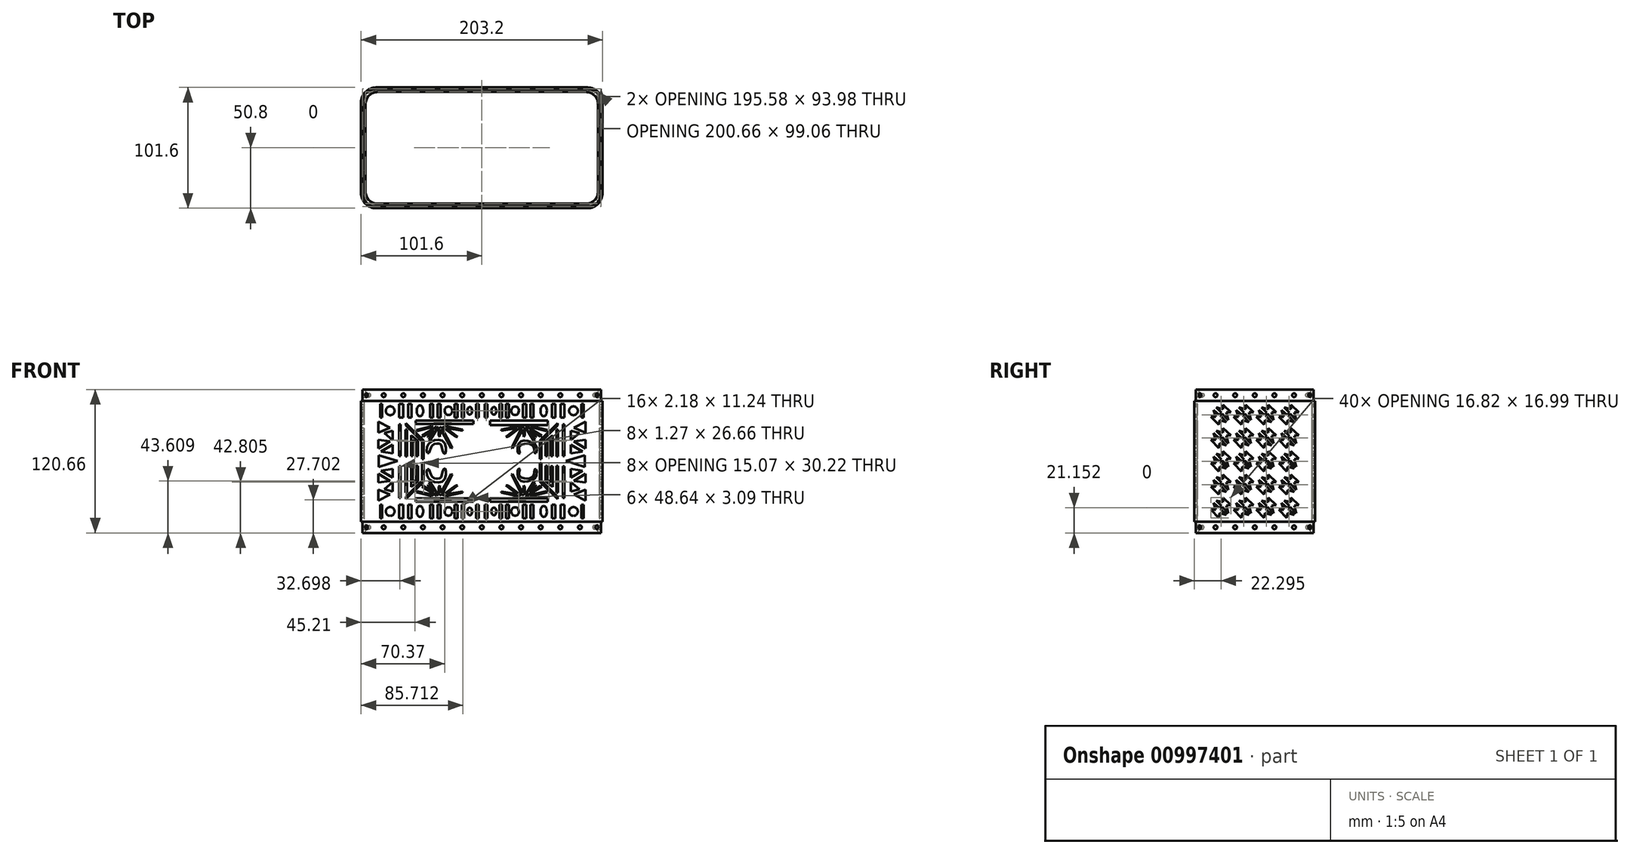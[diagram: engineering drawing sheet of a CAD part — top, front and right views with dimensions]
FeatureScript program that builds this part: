
annotation { "Feature Type Name" : "Feature", "Feature Type Description" : "" }
export const myFeature = defineFeature(function(context is Context, id is Id, definition is map)
    precondition{}
    {
        {
            var Q0;
            Q0=qCreatedBy(makeId("Top.planeOp"),FACE);
            var sketch = newSketch(context, id + "F0", { "sketchPlane" : qUnion([Q0])});
            skLineSegment(sketch, "E0.bottom", {"start": v(-88.9, 50.8) * mm, "end": v(88.9, 50.8) * mm});
            skLineSegment(sketch, "E0.top", {"start": v(-88.9, -50.8) * mm, "end": v(88.9, -50.8) * mm});
            skLineSegment(sketch, "E0.left", {"start": v(-101.6, 38.1) * mm, "end": v(-101.6, -38.1) * mm});
            skLineSegment(sketch, "E0.right", {"start": v(101.6, 38.1) * mm, "end": v(101.6, -38.1) * mm});
            skPoint(sketch, "E1.visualSharp", {"position": v(-101.6, -50.8) * mm});
            skArc(sketch, "E1.filletArc", {"start": v(-101.6, -38.1) * mm, "mid": v(-97.88, -47.08) * mm, "end": v(-88.9, -50.8) * mm});
            skPoint(sketch, "E2.visualSharp", {"position": v(101.6, -50.8) * mm});
            skArc(sketch, "E2.filletArc", {"start": v(88.9, -50.8) * mm, "mid": v(97.88, -47.08) * mm, "end": v(101.6, -38.1) * mm});
            skPoint(sketch, "E3.visualSharp", {"position": v(-101.6, 50.8) * mm});
            skArc(sketch, "E3.filletArc", {"start": v(-88.9, 50.8) * mm, "mid": v(-97.88, 47.08) * mm, "end": v(-101.6, 38.1) * mm});
            skPoint(sketch, "E4.visualSharp", {"position": v(101.6, 50.8) * mm});
            skArc(sketch, "E4.filletArc", {"start": v(101.6, 38.1) * mm, "mid": v(97.88, 47.08) * mm, "end": v(88.9, 50.8) * mm});
            skSolve(sketch);
        }
        {
            var Q0;
            Q0=makeQuery(id+"F0.imprint","IMPRINT",FACE,{"disambiguationData":[TD([[makeQuery(id+"F0.imprint","IMPRINT",EDGE,{"derivedFrom":sQuery(id+"F0.wireOp",EDGE,"E0.bottom")}),-1.0]])]});
            extrude(context, id + "F1", {"entities" : qUnion([Q0]), "depth" : 101.6 * mm, "offsetDistance" : 25.4 * mm});
        }
        {
            var Q0;
            Q0=makeQuery(id+"F1.opExtrude","CAP_FACE",FACE,{"disambiguationData":[OSD([sQuery(id+"F0.wireOp",EDGE,"E0.bottom"),sQuery(id+"F0.wireOp",EDGE,"E0.top"),sQuery(id+"F0.wireOp",EDGE,"E0.left"),sQuery(id+"F0.wireOp",EDGE,"E0.right"),sQuery(id+"F0.wireOp",EDGE,"E1.filletArc"),sQuery(id+"F0.wireOp",EDGE,"E2.filletArc"),sQuery(id+"F0.wireOp",EDGE,"E3.filletArc"),sQuery(id+"F0.wireOp",EDGE,"E4.filletArc")])],"isStart":false});
            var Q1;
            Q1=makeQuery(id+"F1.opExtrude","CAP_FACE",FACE,{"disambiguationData":[OSD([sQuery(id+"F0.wireOp",EDGE,"E0.bottom"),sQuery(id+"F0.wireOp",EDGE,"E0.top"),sQuery(id+"F0.wireOp",EDGE,"E0.left"),sQuery(id+"F0.wireOp",EDGE,"E0.right"),sQuery(id+"F0.wireOp",EDGE,"E1.filletArc"),sQuery(id+"F0.wireOp",EDGE,"E2.filletArc"),sQuery(id+"F0.wireOp",EDGE,"E3.filletArc"),sQuery(id+"F0.wireOp",EDGE,"E4.filletArc")])],"isStart":true});
            shell(context, id + "F2", {"entities" : qUnion([Q0, Q1]), "thickness" : 2.54 * mm});
        }
        {
            var Q0;
            Q0=makeQuery(id+"F1.opExtrude","CAP_FACE",FACE,{"disambiguationData":[OSD([sQuery(id+"F0.wireOp",EDGE,"E0.bottom"),sQuery(id+"F0.wireOp",EDGE,"E0.top"),sQuery(id+"F0.wireOp",EDGE,"E0.left"),sQuery(id+"F0.wireOp",EDGE,"E0.right"),sQuery(id+"F0.wireOp",EDGE,"E1.filletArc"),sQuery(id+"F0.wireOp",EDGE,"E2.filletArc"),sQuery(id+"F0.wireOp",EDGE,"E3.filletArc"),sQuery(id+"F0.wireOp",EDGE,"E4.filletArc")])],"isStart":false});
            var sketch = newSketch(context, id + "F3", { "sketchPlane" : qUnion([Q0])});
            skLineSegment(sketch, "E5.bottom", {"start": v(88.9, -49.53) * mm, "end": v(-88.9, -49.53) * mm});
            skLineSegment(sketch, "E5.top", {"start": v(88.9, 49.53) * mm, "end": v(-88.9, 49.53) * mm});
            skLineSegment(sketch, "E5.left", {"start": v(100.33, -38.1) * mm, "end": v(100.33, 38.1) * mm});
            skLineSegment(sketch, "E5.right", {"start": v(-100.33, -38.1) * mm, "end": v(-100.33, 38.1) * mm});
            skPoint(sketch, "E5.middle", {"position": v(0, 0) * mm});
            skPoint(sketch, "E6.visualSharp", {"position": v(-100.33, 49.53) * mm});
            skArc(sketch, "E6.filletArc", {"start": v(-88.9, 49.53) * mm, "mid": v(-96.98, 46.18) * mm, "end": v(-100.33, 38.1) * mm});
            skPoint(sketch, "E7.visualSharp", {"position": v(100.33, 49.53) * mm});
            skArc(sketch, "E7.filletArc", {"start": v(100.33, 38.1) * mm, "mid": v(96.98, 46.18) * mm, "end": v(88.9, 49.53) * mm});
            skPoint(sketch, "E8.visualSharp", {"position": v(100.33, -49.53) * mm});
            skArc(sketch, "E8.filletArc", {"start": v(88.9, -49.53) * mm, "mid": v(96.98, -46.18) * mm, "end": v(100.33, -38.1) * mm});
            skPoint(sketch, "E9.visualSharp", {"position": v(-100.33, -49.53) * mm});
            skArc(sketch, "E9.filletArc", {"start": v(-100.33, -38.1) * mm, "mid": v(-96.98, -46.18) * mm, "end": v(-88.9, -49.53) * mm});
            skLineSegment(sketch, "E10.bottom", {"start": v(-87.63, 46.99) * mm, "end": v(87.63, 47) * mm});
            skLineSegment(sketch, "E10.top", {"start": v(-87.63, -47) * mm, "end": v(87.63, -46.99) * mm});
            skLineSegment(sketch, "E10.left", {"start": v(-97.8, 36.83) * mm, "end": v(-97.8, -36.83) * mm});
            skLineSegment(sketch, "E10.right", {"start": v(97.8, 36.83) * mm, "end": v(97.8, -36.83) * mm});
            skPoint(sketch, "E11.visualSharp", {"position": v(-97.8, -47) * mm});
            skArc(sketch, "E11.filletArc", {"start": v(-97.8, -36.83) * mm, "mid": v(-94.81, -44.01) * mm, "end": v(-87.63, -47) * mm});
            skPoint(sketch, "E12.visualSharp", {"position": v(-97.8, 46.99) * mm});
            skArc(sketch, "E12.filletArc", {"start": v(-87.63, 47) * mm, "mid": v(-94.81, 44.01) * mm, "end": v(-97.8, 36.83) * mm});
            skPoint(sketch, "E13.visualSharp", {"position": v(97.8, 47) * mm});
            skArc(sketch, "E13.filletArc", {"start": v(97.8, 36.83) * mm, "mid": v(94.81, 44.01) * mm, "end": v(87.63, 47) * mm});
            skPoint(sketch, "E14.visualSharp", {"position": v(97.8, -46.99) * mm});
            skArc(sketch, "E14.filletArc", {"start": v(87.63, -46.99) * mm, "mid": v(94.81, -44.01) * mm, "end": v(97.8, -36.83) * mm});
            skSolve(sketch);
        }
        {
            var Q0;
            Q0=makeQuery(id+"F3.imprint","IMPRINT",FACE,{"disambiguationData":[TD([[makeQuery(id+"F3.imprint","IMPRINT",EDGE,{"derivedFrom":sQuery(id+"F3.wireOp",EDGE,"E10.bottom")}),1.0]])]});
            var Q1;
            Q1=makeQuery(id+"F3.imprint","IMPRINT",FACE,{"disambiguationData":[TD([[makeQuery(id+"F3.imprint","IMPRINT",EDGE,{"derivedFrom":sQuery(id+"F3.wireOp",EDGE,"E5.bottom")}),-1.0]])]});
            extrude(context, id + "F4", {"entities" : qUnion([Q0, Q1]), "operationType" : NewBodyOperationType.ADD, "depth" : 9.52 * mm, "offsetDistance" : 25.4 * mm});
        }
        {
            var Q0;
            Q0=qCreatedBy(makeId("Top.planeOp"),FACE);
            var sketch = newSketch(context, id + "F5", { "sketchPlane" : qUnion([Q0])});
            skLineSegment(sketch, "E15.bottom", {"start": v(-88.9, 49.53) * mm, "end": v(88.9, 49.53) * mm});
            skLineSegment(sketch, "E15.top", {"start": v(-88.9, -49.53) * mm, "end": v(88.9, -49.53) * mm});
            skLineSegment(sketch, "E15.left", {"start": v(-100.33, 38.1) * mm, "end": v(-100.33, -38.1) * mm});
            skLineSegment(sketch, "E15.right", {"start": v(100.33, 38.1) * mm, "end": v(100.33, -38.1) * mm});
            skPoint(sketch, "E15.middle", {"position": v(0, 0) * mm});
            skLineSegment(sketch, "E16.bottom", {"start": v(-87.63, -47) * mm, "end": v(87.63, -46.99) * mm});
            skLineSegment(sketch, "E16.top", {"start": v(-87.63, 46.99) * mm, "end": v(87.63, 47) * mm});
            skLineSegment(sketch, "E16.left", {"start": v(-97.8, -36.83) * mm, "end": v(-97.8, 36.83) * mm});
            skLineSegment(sketch, "E16.right", {"start": v(97.8, -36.83) * mm, "end": v(97.8, 36.83) * mm});
            skPoint(sketch, "E17.visualSharp", {"position": v(97.8, 47) * mm});
            skArc(sketch, "E17.filletArc", {"start": v(97.8, 36.83) * mm, "mid": v(94.81, 44.01) * mm, "end": v(87.63, 47) * mm});
            skPoint(sketch, "E18.visualSharp", {"position": v(-97.8, 46.99) * mm});
            skArc(sketch, "E18.filletArc", {"start": v(-87.63, 46.99) * mm, "mid": v(-94.81, 44.01) * mm, "end": v(-97.79, 36.83) * mm});
            skPoint(sketch, "E19.visualSharp", {"position": v(-97.8, -47) * mm});
            skArc(sketch, "E19.filletArc", {"start": v(-97.8, -36.83) * mm, "mid": v(-94.81, -44.01) * mm, "end": v(-87.63, -47) * mm});
            skPoint(sketch, "E20.visualSharp", {"position": v(97.8, -46.99) * mm});
            skArc(sketch, "E20.filletArc", {"start": v(87.63, -46.99) * mm, "mid": v(94.81, -44.01) * mm, "end": v(97.79, -36.83) * mm});
            skPoint(sketch, "E21.visualSharp", {"position": v(100.33, -49.53) * mm});
            skArc(sketch, "E21.filletArc", {"start": v(88.9, -49.53) * mm, "mid": v(96.98, -46.18) * mm, "end": v(100.33, -38.1) * mm});
            skPoint(sketch, "E22.visualSharp", {"position": v(-100.33, -49.53) * mm});
            skArc(sketch, "E22.filletArc", {"start": v(-100.33, -38.1) * mm, "mid": v(-96.98, -46.18) * mm, "end": v(-88.9, -49.53) * mm});
            skPoint(sketch, "E23.visualSharp", {"position": v(-100.33, 49.53) * mm});
            skArc(sketch, "E23.filletArc", {"start": v(-88.9, 49.53) * mm, "mid": v(-96.98, 46.18) * mm, "end": v(-100.33, 38.1) * mm});
            skPoint(sketch, "E24.visualSharp", {"position": v(100.33, 49.53) * mm});
            skArc(sketch, "E24.filletArc", {"start": v(100.33, 38.1) * mm, "mid": v(96.98, 46.18) * mm, "end": v(88.9, 49.53) * mm});
            skSolve(sketch);
        }
        {
            var Q0;
            Q0 = qSketchRegion(id + "F5", true);
            extrude(context, id + "F6", {"entities" : qUnion([Q0]), "operationType" : NewBodyOperationType.ADD, "oppositeDirection" : true, "depth" : 9.52 * mm, "offsetDistance" : 25.4 * mm});
        }
        {
            var Q0;
            Q0=makeQuery(id+"F1.opExtrude","SWEPT_FACE",FACE,{"disambiguationData":[OSD([sQuery(id+"F0.wireOp",EDGE,"E0.top")])]});
            var sketch = newSketch(context, id + "F7", { "sketchPlane" : qUnion([Q0])});
            skPoint(sketch, "E25", {"position": v(-82.55, 50.8) * mm});
            skPoint(sketch, "E26", {"position": v(82.55, 50.8) * mm});
            skPoint(sketch, "E27", {"position": v(88.9, 50.8) * mm});
            skPoint(sketch, "E28", {"position": v(-88.9, 50.8) * mm});
            skPoint(sketch, "E29", {"position": v(0, 101.6) * mm});
            skPoint(sketch, "E30", {"position": v(0, 97.17) * mm});
            skSolve(sketch);
        }
        {
            var Q0;
            {var subQ0=sQuery(id+"F0.wireOp",EDGE,"E0.top");Q0=makeQuery(id+"F7.imprint","IMPRINT",FACE,{"disambiguationData":[TD([[makeQuery(id+"F7.imprint","IMPRINT",EDGE,{"derivedFrom":makeQuery(id+"F1.opExtrude","CAP_EDGE",EDGE,{"disambiguationData":[OSD([subQ0])],"isStart":true})}),1.0]])]});}
            var sketch = newSketch(context, id + "F8", { "sketchPlane" : qUnion([Q0])});
            skLineSegment(sketch, "E31.bottom", {"start": v(-69.54, 81.8) * mm, "end": v(-68.27, 81.8) * mm});
            skLineSegment(sketch, "E31.top", {"start": v(-69.54, 55.15) * mm, "end": v(-68.27, 55.15) * mm});
            skLineSegment(sketch, "E31.left", {"start": v(-69.54, 81.8) * mm, "end": v(-69.54, 55.15) * mm});
            skLineSegment(sketch, "E31.right", {"start": v(-68.27, 81.8) * mm, "end": v(-68.27, 55.15) * mm});
            skLineSegment(sketch, "E32.bottom", {"start": v(-64.12, 77.24) * mm, "end": v(-62.85, 77.24) * mm});
            skLineSegment(sketch, "E32.top", {"start": v(-64.12, 55) * mm, "end": v(-62.85, 55) * mm});
            skLineSegment(sketch, "E32.left", {"start": v(-64.12, 77.24) * mm, "end": v(-64.12, 55) * mm});
            skLineSegment(sketch, "E32.right", {"start": v(-62.85, 77.24) * mm, "end": v(-62.85, 55) * mm});
            skLineSegment(sketch, "E33", {"start": v(-59.53, 55.07) * mm, "end": v(-59.53, 72.59) * mm});
            skLineSegment(sketch, "E34", {"start": v(-59.53, 72.59) * mm, "end": v(-53.58, 67.88) * mm});
            skLineSegment(sketch, "E35", {"start": v(-53.58, 67.88) * mm, "end": v(-53.58, 55) * mm});
            skLineSegment(sketch, "E36", {"start": v(-53.58, 55) * mm, "end": v(-55.15, 55) * mm});
            skLineSegment(sketch, "E37", {"start": v(-55.15, 55) * mm, "end": v(-55.15, 66.64) * mm});
            skLineSegment(sketch, "E38", {"start": v(-55.15, 66.64) * mm, "end": v(-58.16, 68.8) * mm});
            skLineSegment(sketch, "E39", {"start": v(-59.53, 55.07) * mm, "end": v(-58.16, 55.07) * mm});
            skLineSegment(sketch, "E40", {"start": v(-58.16, 55.07) * mm, "end": v(-58.16, 68.8) * mm});
            skLineSegment(sketch, "E41", {"start": v(-50.14, 52.56) * mm, "end": v(-50.14, 67.28) * mm});
            skLineSegment(sketch, "E42", {"start": v(-50.14, 67.28) * mm, "end": v(-63.92, 80.98) * mm});
            skLineSegment(sketch, "E43", {"start": v(-63.92, 80.98) * mm, "end": v(-63.92, 82.78) * mm});
            skLineSegment(sketch, "E44", {"start": v(-63.92, 82.78) * mm, "end": v(-48.86, 68.23) * mm});
            skLineSegment(sketch, "E45", {"start": v(-48.86, 68.23) * mm, "end": v(-48.86, 52.56) * mm});
            skLineSegment(sketch, "E46", {"start": v(-48.86, 52.56) * mm, "end": v(-50.14, 52.56) * mm});
            skLineSegment(sketch, "E47.bottom", {"start": v(-55.55, 82.03) * mm, "end": v(-6.91, 82.03) * mm});
            skLineSegment(sketch, "E47.top", {"start": v(-55.55, 85.13) * mm, "end": v(-6.91, 85.13) * mm});
            skLineSegment(sketch, "E47.left", {"start": v(-55.55, 82.03) * mm, "end": v(-55.55, 85.13) * mm});
            skLineSegment(sketch, "E47.right", {"start": v(-6.91, 82.03) * mm, "end": v(-6.91, 85.13) * mm});
            skLineSegment(sketch, "E48", {"start": v(-55.1, 76.98) * mm, "end": v(-42.24, 80.13) * mm});
            skLineSegment(sketch, "E49", {"start": v(-42.24, 80.13) * mm, "end": v(-40.9, 79.45) * mm});
            skLineSegment(sketch, "E50", {"start": v(-40.9, 79.45) * mm, "end": v(-54.58, 76.07) * mm});
            skLineSegment(sketch, "E51", {"start": v(-54.58, 76.07) * mm, "end": v(-55.1, 76.98) * mm});
            skLineSegment(sketch, "E52", {"start": v(-50.33, 72.34) * mm, "end": v(-49.32, 71.33) * mm});
            skLineSegment(sketch, "E53", {"start": v(-49.32, 71.33) * mm, "end": v(-40.54, 77.24) * mm});
            skLineSegment(sketch, "E54", {"start": v(-40.54, 77.24) * mm, "end": v(-45.9, 71.84) * mm});
            skLineSegment(sketch, "E55", {"start": v(-45.9, 71.84) * mm, "end": v(-45.04, 70.98) * mm});
            skLineSegment(sketch, "E56", {"start": v(-45.04, 70.98) * mm, "end": v(-40.01, 76.03) * mm});
            skLineSegment(sketch, "E57", {"start": v(-40.01, 76.03) * mm, "end": v(-44.6, 68.93) * mm});
            skLineSegment(sketch, "E58", {"start": v(-44.6, 68.93) * mm, "end": v(-43.9, 67.87) * mm});
            skLineSegment(sketch, "E59", {"start": v(-43.9, 67.87) * mm, "end": v(-36.86, 79.28) * mm});
            skLineSegment(sketch, "E60", {"start": v(-36.86, 79.28) * mm, "end": v(-37.94, 79.94) * mm});
            skLineSegment(sketch, "E61", {"start": v(-37.94, 79.94) * mm, "end": v(-50.33, 72.34) * mm});
            skLineSegment(sketch, "E62", {"start": v(-36.28, 72.34) * mm, "end": v(-35.26, 71.33) * mm});
            skLineSegment(sketch, "E63", {"start": v(-34.02, 79.8) * mm, "end": v(-36.11, 78.38) * mm});
            skLineSegment(sketch, "E64", {"start": v(-36.11, 78.38) * mm, "end": v(-36.28, 72.34) * mm});
            skLineSegment(sketch, "E65", {"start": v(-34.02, 79.8) * mm, "end": v(-24.97, 62.28) * mm});
            skLineSegment(sketch, "E66", {"start": v(-24.97, 62.28) * mm, "end": v(-25.62, 61.62) * mm});
            skLineSegment(sketch, "E67", {"start": v(-22.03, 71.33) * mm, "end": v(-20.4, 71.33) * mm});
            skLineSegment(sketch, "E68", {"start": v(-20.4, 71.33) * mm, "end": v(-29.91, 78.67) * mm});
            skLineSegment(sketch, "E69", {"start": v(-29.91, 78.67) * mm, "end": v(-16.35, 76.46) * mm});
            skLineSegment(sketch, "E70", {"start": v(-16.35, 76.46) * mm, "end": v(-16.35, 77.5) * mm});
            skLineSegment(sketch, "E71", {"start": v(-16.35, 77.5) * mm, "end": v(-29.9, 80.27) * mm});
            skLineSegment(sketch, "E72", {"start": v(-29.9, 80.27) * mm, "end": v(-32.77, 79.37) * mm});
            skFitSpline(sketch, "E73", {"points": [v(-45.65, 57.64) * mm, v(-45.68, 63.84) * mm, v(-39.17, 68.5) * mm, v(-31.43, 66.27) * mm, v(-30.64, 57.48) * mm, v(-32.02, 57.42) * mm, v(-33.93, 63.5) * mm, v(-35.4, 65.37) * mm, v(-39.79, 65.41) * mm, v(-43.04, 61.77) * mm, v(-44.66, 57.59) * mm, v(-45.65, 57.64) * mm]});
            skLineSegment(sketch, "E74", {"start": v(-25.62, 61.62) * mm, "end": v(-34.64, 77.63) * mm});
            skLineSegment(sketch, "E75", {"start": v(-34.64, 77.63) * mm, "end": v(-35.26, 71.33) * mm});
            skLineSegment(sketch, "E76", {"start": v(-22.03, 71.33) * mm, "end": v(-32.77, 79.37) * mm});
            skLineSegment(sketch, "E77.MirrorCS", {"start": v(50.33, 72.34) * mm, "end": v(49.32, 71.33) * mm});
            skLineSegment(sketch, "E78.MirrorCS", {"start": v(36.86, 79.28) * mm, "end": v(37.94, 79.94) * mm});
            skLineSegment(sketch, "E79.MirrorCS", {"start": v(63.92, 80.98) * mm, "end": v(63.92, 82.78) * mm});
            skLineSegment(sketch, "E80.MirrorCS", {"start": v(45.9, 71.84) * mm, "end": v(45.04, 70.98) * mm});
            skLineSegment(sketch, "E81.MirrorCS", {"start": v(59.53, 55.07) * mm, "end": v(58.16, 55.07) * mm});
            skLineSegment(sketch, "E82.MirrorCS", {"start": v(55.55, 81.06) * mm, "end": v(55.55, 85.13) * mm});
            skLineSegment(sketch, "E83.MirrorCS", {"start": v(36.28, 72.34) * mm, "end": v(35.26, 71.33) * mm});
            skLineSegment(sketch, "E84.MirrorCS", {"start": v(53.58, 55) * mm, "end": v(55.15, 55) * mm});
            skLineSegment(sketch, "E85.MirrorCS", {"start": v(29.9, 80.27) * mm, "end": v(32.77, 79.37) * mm});
            skLineSegment(sketch, "E86.MirrorCS", {"start": v(34.64, 77.63) * mm, "end": v(35.26, 71.33) * mm});
            skLineSegment(sketch, "E87.MirrorCS", {"start": v(64.12, 55) * mm, "end": v(62.85, 55) * mm});
            skLineSegment(sketch, "E88.MirrorCS", {"start": v(69.54, 55.15) * mm, "end": v(68.27, 55.15) * mm});
            skLineSegment(sketch, "E89.MirrorCS", {"start": v(44.6, 68.93) * mm, "end": v(43.9, 67.87) * mm});
            skLineSegment(sketch, "E90.MirrorCS", {"start": v(54.58, 76.07) * mm, "end": v(55.1, 76.98) * mm});
            skLineSegment(sketch, "E91.MirrorCS", {"start": v(24.97, 62.28) * mm, "end": v(25.62, 61.62) * mm});
            skLineSegment(sketch, "E92.MirrorCS", {"start": v(16.35, 76.46) * mm, "end": v(16.35, 77.5) * mm});
            skLineSegment(sketch, "E93.MirrorCS", {"start": v(6.91, 81.06) * mm, "end": v(6.91, 85.13) * mm});
            skLineSegment(sketch, "E94.MirrorCS", {"start": v(55.15, 66.64) * mm, "end": v(58.16, 68.8) * mm});
            skLineSegment(sketch, "E95.MirrorCS", {"start": v(45.04, 70.98) * mm, "end": v(40.01, 76.03) * mm});
            skLineSegment(sketch, "E96.MirrorCS", {"start": v(59.53, 72.59) * mm, "end": v(53.58, 67.88) * mm});
            skLineSegment(sketch, "E97.MirrorCS", {"start": v(64.12, 77.24) * mm, "end": v(62.85, 77.24) * mm});
            skLineSegment(sketch, "E98.MirrorCS", {"start": v(22.03, 71.33) * mm, "end": v(20.4, 71.33) * mm});
            skLineSegment(sketch, "E99.MirrorCS", {"start": v(36.11, 78.38) * mm, "end": v(36.28, 72.34) * mm});
            skLineSegment(sketch, "E100.MirrorCS", {"start": v(69.54, 81.8) * mm, "end": v(68.27, 81.8) * mm});
            skLineSegment(sketch, "E101.MirrorCS", {"start": v(34.02, 79.8) * mm, "end": v(36.11, 78.38) * mm});
            skLineSegment(sketch, "E102.MirrorCS", {"start": v(42.24, 80.13) * mm, "end": v(40.9, 79.45) * mm});
            skLineSegment(sketch, "E103.MirrorCS", {"start": v(48.86, 52.56) * mm, "end": v(50.14, 52.56) * mm});
            skLineSegment(sketch, "E104.MirrorCS", {"start": v(49.32, 71.33) * mm, "end": v(40.54, 77.24) * mm});
            skLineSegment(sketch, "E105.MirrorCS", {"start": v(64.12, 77.24) * mm, "end": v(64.12, 55) * mm});
            skFitSpline(sketch, "E106.MirrorC", {"points": [v(45.65, 57.64) * mm, v(45.68, 63.84) * mm, v(38.4, 67.98) * mm, v(31.43, 66.27) * mm, v(30.64, 57.48) * mm, v(32.02, 57.42) * mm, v(31.25, 62.15) * mm, v(35.4, 65.37) * mm, v(39.79, 65.41) * mm, v(43.58, 62.94) * mm, v(44.66, 57.59) * mm, v(45.65, 57.64) * mm]});
            skLineSegment(sketch, "E107.MirrorCS", {"start": v(55.55, 81.06) * mm, "end": v(6.91, 81.06) * mm});
            skLineSegment(sketch, "E108.MirrorCS", {"start": v(40.9, 79.45) * mm, "end": v(54.58, 76.07) * mm});
            skLineSegment(sketch, "E109.MirrorCS", {"start": v(55.15, 55) * mm, "end": v(55.15, 66.64) * mm});
            skLineSegment(sketch, "E110.MirrorCS", {"start": v(58.16, 55.07) * mm, "end": v(58.16, 68.8) * mm});
            skLineSegment(sketch, "E111.MirrorCS", {"start": v(55.55, 85.13) * mm, "end": v(6.91, 85.13) * mm});
            skLineSegment(sketch, "E112.MirrorCS", {"start": v(63.92, 82.78) * mm, "end": v(48.86, 68.23) * mm});
            skLineSegment(sketch, "E113.MirrorCS", {"start": v(34.02, 79.8) * mm, "end": v(24.97, 62.28) * mm});
            skLineSegment(sketch, "E114.MirrorCS", {"start": v(50.14, 67.28) * mm, "end": v(63.92, 80.98) * mm});
            skLineSegment(sketch, "E115.MirrorCS", {"start": v(59.53, 55.07) * mm, "end": v(59.53, 72.59) * mm});
            skLineSegment(sketch, "E116.MirrorCS", {"start": v(68.27, 81.8) * mm, "end": v(68.27, 55.15) * mm});
            skLineSegment(sketch, "E117.MirrorCS", {"start": v(40.54, 77.24) * mm, "end": v(45.9, 71.84) * mm});
            skLineSegment(sketch, "E118.MirrorCS", {"start": v(62.85, 77.24) * mm, "end": v(62.85, 55) * mm});
            skLineSegment(sketch, "E119.MirrorCS", {"start": v(16.35, 77.5) * mm, "end": v(29.9, 80.27) * mm});
            skLineSegment(sketch, "E120.MirrorCS", {"start": v(29.91, 78.67) * mm, "end": v(16.35, 76.46) * mm});
            skLineSegment(sketch, "E121.MirrorCS", {"start": v(40.01, 76.03) * mm, "end": v(44.6, 68.93) * mm});
            skLineSegment(sketch, "E122.MirrorCS", {"start": v(25.62, 61.62) * mm, "end": v(34.64, 77.63) * mm});
            skLineSegment(sketch, "E123.MirrorCS", {"start": v(43.9, 67.87) * mm, "end": v(36.86, 79.28) * mm});
            skLineSegment(sketch, "E124.MirrorCS", {"start": v(69.54, 81.8) * mm, "end": v(69.54, 55.15) * mm});
            skLineSegment(sketch, "E125.MirrorCS", {"start": v(48.86, 68.23) * mm, "end": v(48.86, 52.56) * mm});
            skLineSegment(sketch, "E126.MirrorCS", {"start": v(50.14, 52.56) * mm, "end": v(50.14, 67.28) * mm});
            skLineSegment(sketch, "E127.MirrorCS", {"start": v(55.1, 76.98) * mm, "end": v(42.24, 80.13) * mm});
            skLineSegment(sketch, "E128.MirrorCS", {"start": v(37.94, 79.94) * mm, "end": v(50.33, 72.34) * mm});
            skLineSegment(sketch, "E129.MirrorCS", {"start": v(22.03, 71.33) * mm, "end": v(32.77, 79.37) * mm});
            skLineSegment(sketch, "E130.MirrorCS", {"start": v(53.58, 67.88) * mm, "end": v(53.58, 55) * mm});
            skLineSegment(sketch, "E131.MirrorCS", {"start": v(20.4, 71.33) * mm, "end": v(29.91, 78.67) * mm});
            skLineSegment(sketch, "E132", {"start": v(0, 50.88) * mm, "end": v(-88.8, 50.88) * mm, "construction": true});
            skLineSegment(sketch, "E133.MirrorCS", {"start": v(-48.86, 49.19) * mm, "end": v(-50.14, 49.19) * mm});
            skLineSegment(sketch, "E134.MirrorCS", {"start": v(-48.86, 33.53) * mm, "end": v(-48.86, 49.19) * mm});
            skLineSegment(sketch, "E135.MirrorCS", {"start": v(-50.14, 49.19) * mm, "end": v(-50.14, 34.47) * mm});
            skLineSegment(sketch, "E136.MirrorCS", {"start": v(-53.58, 46.75) * mm, "end": v(-55.15, 46.75) * mm});
            skLineSegment(sketch, "E137.MirrorCS", {"start": v(-55.15, 46.75) * mm, "end": v(-55.15, 35.11) * mm});
            skLineSegment(sketch, "E138.MirrorCS", {"start": v(-53.58, 33.87) * mm, "end": v(-53.58, 46.75) * mm});
            skLineSegment(sketch, "E139.MirrorCS", {"start": v(-58.16, 46.68) * mm, "end": v(-58.16, 32.95) * mm});
            skLineSegment(sketch, "E140.MirrorCS", {"start": v(-59.53, 46.68) * mm, "end": v(-58.16, 46.68) * mm});
            skLineSegment(sketch, "E141.MirrorCS", {"start": v(-59.53, 46.68) * mm, "end": v(-59.53, 29.16) * mm});
            skLineSegment(sketch, "E142.MirrorCS", {"start": v(-62.85, 24.52) * mm, "end": v(-62.85, 46.76) * mm});
            skLineSegment(sketch, "E143.MirrorCS", {"start": v(-64.12, 24.52) * mm, "end": v(-64.12, 46.76) * mm});
            skLineSegment(sketch, "E144.MirrorCS", {"start": v(-64.12, 46.76) * mm, "end": v(-62.85, 46.76) * mm});
            skLineSegment(sketch, "E145.MirrorCS", {"start": v(-69.54, 46.6) * mm, "end": v(-68.27, 46.6) * mm});
            skLineSegment(sketch, "E146.MirrorCS", {"start": v(-69.54, 19.94) * mm, "end": v(-69.54, 46.6) * mm});
            skLineSegment(sketch, "E147.MirrorCS", {"start": v(-68.27, 19.94) * mm, "end": v(-68.27, 46.6) * mm});
            skLineSegment(sketch, "E148.MirrorCS", {"start": v(-34.02, 21.96) * mm, "end": v(-36.11, 23.37) * mm});
            skLineSegment(sketch, "E149.MirrorCS", {"start": v(-29.9, 21.48) * mm, "end": v(-32.77, 22.38) * mm});
            skLineSegment(sketch, "E150.MirrorCS", {"start": v(-50.33, 29.41) * mm, "end": v(-49.32, 30.42) * mm});
            skLineSegment(sketch, "E151.MirrorCS", {"start": v(-55.55, 19.72) * mm, "end": v(-55.55, 16.63) * mm});
            skLineSegment(sketch, "E152.MirrorCS", {"start": v(-16.35, 25.3) * mm, "end": v(-16.35, 24.25) * mm});
            skLineSegment(sketch, "E153.MirrorCS", {"start": v(-22.03, 30.42) * mm, "end": v(-20.4, 30.42) * mm});
            skLineSegment(sketch, "E154.MirrorCS", {"start": v(-24.97, 39.48) * mm, "end": v(-25.62, 40.13) * mm});
            skLineSegment(sketch, "E155.MirrorCS", {"start": v(-69.54, 19.94) * mm, "end": v(-68.27, 19.94) * mm});
            skLineSegment(sketch, "E156.MirrorCS", {"start": v(-63.92, 20.77) * mm, "end": v(-63.92, 18.97) * mm});
            skLineSegment(sketch, "E157.MirrorCS", {"start": v(-6.91, 19.72) * mm, "end": v(-6.91, 16.63) * mm});
            skLineSegment(sketch, "E158.MirrorCS", {"start": v(-55.15, 35.11) * mm, "end": v(-58.16, 32.95) * mm});
            skLineSegment(sketch, "E159.MirrorCS", {"start": v(-44.6, 32.83) * mm, "end": v(-43.9, 33.88) * mm});
            skLineSegment(sketch, "E160.MirrorCS", {"start": v(-42.24, 21.62) * mm, "end": v(-40.9, 22.3) * mm});
            skLineSegment(sketch, "E161.MirrorCS", {"start": v(-36.28, 29.41) * mm, "end": v(-35.26, 30.42) * mm});
            skLineSegment(sketch, "E162.MirrorCS", {"start": v(-45.9, 29.92) * mm, "end": v(-45.04, 30.78) * mm});
            skLineSegment(sketch, "E163.MirrorCS", {"start": v(-64.12, 24.52) * mm, "end": v(-62.85, 24.52) * mm});
            skLineSegment(sketch, "E164.MirrorCS", {"start": v(-54.58, 25.68) * mm, "end": v(-55.1, 24.77) * mm});
            skLineSegment(sketch, "E165.MirrorCS", {"start": v(-36.86, 22.48) * mm, "end": v(-37.94, 21.81) * mm});
            skLineSegment(sketch, "E166.MirrorCS", {"start": v(-40.01, 25.72) * mm, "end": v(-44.6, 32.83) * mm});
            skLineSegment(sketch, "E167.MirrorCS", {"start": v(-36.11, 23.37) * mm, "end": v(-36.28, 29.41) * mm});
            skFitSpline(sketch, "E168.MirrorC", {"points": [v(-45.65, 44.1) * mm, v(-45.68, 37.91) * mm, v(-39.17, 33.24) * mm, v(-31.43, 35.48) * mm, v(-30.64, 44.27) * mm, v(-32.02, 44.33) * mm, v(-33.93, 38.25) * mm, v(-35.4, 36.38) * mm, v(-39.79, 36.34) * mm, v(-43.04, 39.98) * mm, v(-44.66, 44.16) * mm, v(-45.65, 44.1) * mm]});
            skLineSegment(sketch, "E169.MirrorCS", {"start": v(-40.54, 24.52) * mm, "end": v(-45.9, 29.92) * mm});
            skLineSegment(sketch, "E170.MirrorCS", {"start": v(-34.64, 24.12) * mm, "end": v(-35.26, 30.42) * mm});
            skLineSegment(sketch, "E171.MirrorCS", {"start": v(-29.91, 23.08) * mm, "end": v(-16.35, 25.3) * mm});
            skLineSegment(sketch, "E172.MirrorCS", {"start": v(-16.35, 24.25) * mm, "end": v(-29.9, 21.48) * mm});
            skLineSegment(sketch, "E173.MirrorCS", {"start": v(-55.55, 19.72) * mm, "end": v(-6.91, 19.72) * mm});
            skLineSegment(sketch, "E174.MirrorCS", {"start": v(-25.62, 40.13) * mm, "end": v(-34.64, 24.12) * mm});
            skLineSegment(sketch, "E175.MirrorCS", {"start": v(-59.53, 29.16) * mm, "end": v(-53.58, 33.87) * mm});
            skLineSegment(sketch, "E176.MirrorCS", {"start": v(-43.9, 33.88) * mm, "end": v(-36.86, 22.48) * mm});
            skLineSegment(sketch, "E177.MirrorCS", {"start": v(-50.14, 34.47) * mm, "end": v(-63.92, 20.77) * mm});
            skLineSegment(sketch, "E178.MirrorCS", {"start": v(-55.1, 24.77) * mm, "end": v(-42.24, 21.62) * mm});
            skLineSegment(sketch, "E179.MirrorCS", {"start": v(-34.02, 21.96) * mm, "end": v(-24.97, 39.48) * mm});
            skLineSegment(sketch, "E180.MirrorCS", {"start": v(-63.92, 18.97) * mm, "end": v(-48.86, 33.53) * mm});
            skLineSegment(sketch, "E181.MirrorCS", {"start": v(-40.9, 22.3) * mm, "end": v(-54.58, 25.68) * mm});
            skLineSegment(sketch, "E182.MirrorCS", {"start": v(-37.94, 21.81) * mm, "end": v(-50.33, 29.41) * mm});
            skLineSegment(sketch, "E183.MirrorCS", {"start": v(-55.55, 16.63) * mm, "end": v(-6.91, 16.63) * mm});
            skLineSegment(sketch, "E184.MirrorCS", {"start": v(-20.4, 30.42) * mm, "end": v(-29.91, 23.08) * mm});
            skLineSegment(sketch, "E185.MirrorCS", {"start": v(-49.32, 30.42) * mm, "end": v(-40.54, 24.52) * mm});
            skLineSegment(sketch, "E186.MirrorCS", {"start": v(-22.03, 30.42) * mm, "end": v(-32.77, 22.38) * mm});
            skLineSegment(sketch, "E187.MirrorCS", {"start": v(-45.04, 30.78) * mm, "end": v(-40.01, 25.72) * mm});
            skLineSegment(sketch, "E188.MirrorCS", {"start": v(64.12, 46.76) * mm, "end": v(62.85, 46.76) * mm});
            skLineSegment(sketch, "E189.MirrorCS", {"start": v(64.12, 24.52) * mm, "end": v(62.85, 24.52) * mm});
            skLineSegment(sketch, "E190.MirrorCS", {"start": v(34.02, 21.96) * mm, "end": v(36.11, 23.37) * mm});
            skLineSegment(sketch, "E191.MirrorCS", {"start": v(24.97, 39.48) * mm, "end": v(25.62, 40.13) * mm});
            skLineSegment(sketch, "E192.MirrorCS", {"start": v(42.24, 21.62) * mm, "end": v(40.9, 22.3) * mm});
            skLineSegment(sketch, "E193.MirrorCS", {"start": v(36.28, 29.41) * mm, "end": v(35.26, 30.42) * mm});
            skLineSegment(sketch, "E194.MirrorCS", {"start": v(50.33, 29.41) * mm, "end": v(49.32, 30.42) * mm});
            skLineSegment(sketch, "E195.MirrorCS", {"start": v(69.54, 46.6) * mm, "end": v(68.27, 46.6) * mm});
            skLineSegment(sketch, "E196.MirrorCS", {"start": v(44.6, 32.83) * mm, "end": v(43.9, 33.88) * mm});
            skLineSegment(sketch, "E197.MirrorCS", {"start": v(16.35, 25.3) * mm, "end": v(16.35, 24.25) * mm});
            skLineSegment(sketch, "E198.MirrorCS", {"start": v(55.15, 35.11) * mm, "end": v(58.16, 32.95) * mm});
            skLineSegment(sketch, "E199.MirrorCS", {"start": v(54.58, 25.68) * mm, "end": v(55.1, 24.77) * mm});
            skLineSegment(sketch, "E200.MirrorCS", {"start": v(45.9, 29.92) * mm, "end": v(45.04, 30.78) * mm});
            skLineSegment(sketch, "E201.MirrorCS", {"start": v(59.53, 46.68) * mm, "end": v(58.16, 46.68) * mm});
            skLineSegment(sketch, "E202.MirrorCS", {"start": v(69.54, 19.94) * mm, "end": v(68.27, 19.94) * mm});
            skLineSegment(sketch, "E203.MirrorCS", {"start": v(29.9, 21.48) * mm, "end": v(32.77, 22.38) * mm});
            skLineSegment(sketch, "E204.MirrorCS", {"start": v(63.92, 20.77) * mm, "end": v(63.92, 18.97) * mm});
            skLineSegment(sketch, "E205.MirrorCS", {"start": v(53.58, 46.75) * mm, "end": v(55.15, 46.75) * mm});
            skLineSegment(sketch, "E206.MirrorCS", {"start": v(36.86, 22.48) * mm, "end": v(37.94, 21.81) * mm});
            skLineSegment(sketch, "E207.MirrorCS", {"start": v(22.03, 30.42) * mm, "end": v(20.4, 30.42) * mm});
            skLineSegment(sketch, "E208.MirrorCS", {"start": v(58.16, 46.68) * mm, "end": v(58.16, 32.95) * mm});
            skLineSegment(sketch, "E209.MirrorCS", {"start": v(22.03, 30.42) * mm, "end": v(32.77, 22.38) * mm});
            skLineSegment(sketch, "E210.MirrorCS", {"start": v(40.01, 25.72) * mm, "end": v(44.6, 32.83) * mm});
            skLineSegment(sketch, "E211.MirrorCS", {"start": v(53.58, 33.87) * mm, "end": v(53.58, 46.75) * mm});
            skLineSegment(sketch, "E212.MirrorCS", {"start": v(16.35, 24.25) * mm, "end": v(29.9, 21.48) * mm});
            skLineSegment(sketch, "E213.MirrorCS", {"start": v(40.9, 22.3) * mm, "end": v(54.58, 25.68) * mm});
            skLineSegment(sketch, "E214.MirrorCS", {"start": v(20.4, 30.42) * mm, "end": v(29.91, 23.08) * mm});
            skLineSegment(sketch, "E215.MirrorCS", {"start": v(29.91, 23.08) * mm, "end": v(16.35, 25.3) * mm});
            skLineSegment(sketch, "E216.MirrorCS", {"start": v(55.15, 46.75) * mm, "end": v(55.15, 35.11) * mm});
            skLineSegment(sketch, "E217.MirrorCS", {"start": v(69.54, 19.94) * mm, "end": v(69.54, 46.6) * mm});
            skLineSegment(sketch, "E218.MirrorCS", {"start": v(25.62, 40.13) * mm, "end": v(34.64, 24.12) * mm});
            skLineSegment(sketch, "E219.MirrorCS", {"start": v(40.54, 24.52) * mm, "end": v(45.9, 29.92) * mm});
            skLineSegment(sketch, "E220.MirrorCS", {"start": v(55.55, 19.7) * mm, "end": v(6.91, 19.7) * mm});
            skLineSegment(sketch, "E221.MirrorCS", {"start": v(49.32, 30.42) * mm, "end": v(40.54, 24.52) * mm});
            skLineSegment(sketch, "E222.MirrorCS", {"start": v(37.94, 21.81) * mm, "end": v(50.33, 29.41) * mm});
            skLineSegment(sketch, "E223.MirrorCS", {"start": v(63.92, 18.97) * mm, "end": v(48.86, 33.53) * mm});
            skLineSegment(sketch, "E224.MirrorCS", {"start": v(64.12, 24.52) * mm, "end": v(64.12, 46.76) * mm});
            skLineSegment(sketch, "E225.MirrorCS", {"start": v(59.53, 29.16) * mm, "end": v(53.58, 33.87) * mm});
            skLineSegment(sketch, "E226.MirrorCS", {"start": v(48.86, 49.19) * mm, "end": v(50.14, 49.19) * mm});
            skLineSegment(sketch, "E227.MirrorCS", {"start": v(55.1, 24.77) * mm, "end": v(42.24, 21.62) * mm});
            skLineSegment(sketch, "E228.MirrorCS", {"start": v(68.27, 19.94) * mm, "end": v(68.27, 46.6) * mm});
            skLineSegment(sketch, "E229.MirrorCS", {"start": v(59.53, 46.68) * mm, "end": v(59.53, 29.16) * mm});
            skLineSegment(sketch, "E230.MirrorCS", {"start": v(43.9, 33.88) * mm, "end": v(36.86, 22.48) * mm});
            skLineSegment(sketch, "E231.MirrorCS", {"start": v(48.86, 33.53) * mm, "end": v(48.86, 49.19) * mm});
            skLineSegment(sketch, "E232.MirrorCS", {"start": v(36.11, 23.37) * mm, "end": v(36.28, 29.41) * mm});
            skLineSegment(sketch, "E233.MirrorCS", {"start": v(62.85, 24.52) * mm, "end": v(62.85, 46.76) * mm});
            skFitSpline(sketch, "E234.MirrorC", {"points": [v(45.65, 44.1) * mm, v(45.68, 37.91) * mm, v(38.4, 33.78) * mm, v(31.43, 35.48) * mm, v(30.64, 44.27) * mm, v(32.02, 44.33) * mm, v(31.25, 39.6) * mm, v(35.4, 36.38) * mm, v(39.79, 36.34) * mm, v(43.58, 38.81) * mm, v(44.66, 44.16) * mm, v(45.65, 44.1) * mm]});
            skLineSegment(sketch, "E235.MirrorCS", {"start": v(45.04, 30.78) * mm, "end": v(40.01, 25.72) * mm});
            skLineSegment(sketch, "E236.MirrorCS", {"start": v(50.14, 49.19) * mm, "end": v(50.14, 34.47) * mm});
            skLineSegment(sketch, "E237.MirrorCS", {"start": v(34.64, 24.12) * mm, "end": v(35.26, 30.42) * mm});
            skLineSegment(sketch, "E238.MirrorCS", {"start": v(50.14, 34.47) * mm, "end": v(63.92, 20.77) * mm});
            skLineSegment(sketch, "E239.MirrorCS", {"start": v(34.02, 21.96) * mm, "end": v(24.97, 39.48) * mm});
            skLineSegment(sketch, "E240", {"start": v(0, 102) * mm, "end": v(0, 0) * mm, "construction": true});
            skLineSegment(sketch, "E241", {"start": v(-88.8, 8.52) * mm, "end": v(0, 8.52) * mm, "construction": true});
            skLineSegment(sketch, "E242.bottom", {"start": v(-83.9, 14.14) * mm, "end": v(-85.54, 14.14) * mm});
            skLineSegment(sketch, "E242.top", {"start": v(-83.9, 2.9) * mm, "end": v(-85.54, 2.9) * mm});
            skLineSegment(sketch, "E242.left", {"start": v(-83.9, 14.14) * mm, "end": v(-83.9, 2.9) * mm});
            skLineSegment(sketch, "E242.right", {"start": v(-85.54, 14.14) * mm, "end": v(-85.54, 2.9) * mm});
            skPoint(sketch, "E242.middle", {"position": v(-84.73, 8.52) * mm});
            skCircle(sketch, "E243", {"center": v(-77.1, 8.52) * mm, "radius": 3.7 * mm});
            skLineSegment(sketch, "E244.bottom", {"start": v(-69.48, 14.14) * mm, "end": v(-66.22, 14.14) * mm});
            skLineSegment(sketch, "E244.top", {"start": v(-69.48, 2.9) * mm, "end": v(-66.22, 2.9) * mm});
            skLineSegment(sketch, "E244.left", {"start": v(-69.48, 14.14) * mm, "end": v(-69.48, 2.9) * mm});
            skLineSegment(sketch, "E244.right", {"start": v(-66.22, 14.14) * mm, "end": v(-66.22, 2.9) * mm});
            skPoint(sketch, "E244.middle", {"position": v(-67.85, 8.52) * mm});
            skLineSegment(sketch, "E245.bottom", {"start": v(-61.86, 14.14) * mm, "end": v(-59.14, 14.14) * mm});
            skLineSegment(sketch, "E245.top", {"start": v(-61.86, 2.9) * mm, "end": v(-59.14, 2.9) * mm});
            skLineSegment(sketch, "E245.left", {"start": v(-61.86, 14.14) * mm, "end": v(-61.86, 2.9) * mm});
            skLineSegment(sketch, "E245.right", {"start": v(-59.14, 14.14) * mm, "end": v(-59.14, 2.9) * mm});
            skPoint(sketch, "E245.middle", {"position": v(-60.5, 8.52) * mm});
            skEllipse(sketch, "E246", {"center": v(-52.06, 8.52) * mm, "majorRadius": 4.63 * mm, "minorRadius": 2.73 * mm, "majorAxis": v(0, 1)});
            skLineSegment(sketch, "E247.bottom", {"start": v(-43.57, 14.14) * mm, "end": v(-40.96, 14.14) * mm});
            skLineSegment(sketch, "E247.top", {"start": v(-43.57, 2.9) * mm, "end": v(-40.96, 2.9) * mm});
            skLineSegment(sketch, "E247.left", {"start": v(-43.57, 14.14) * mm, "end": v(-43.57, 2.9) * mm});
            skLineSegment(sketch, "E247.right", {"start": v(-40.96, 14.14) * mm, "end": v(-40.96, 2.9) * mm});
            skPoint(sketch, "E247.middle", {"position": v(-42.27, 8.52) * mm});
            skLineSegment(sketch, "E248.bottom", {"start": v(-37.26, 14.14) * mm, "end": v(-34.67, 14.14) * mm});
            skLineSegment(sketch, "E248.top", {"start": v(-37.26, 2.9) * mm, "end": v(-34.67, 2.9) * mm});
            skLineSegment(sketch, "E248.left", {"start": v(-37.26, 14.14) * mm, "end": v(-37.26, 2.9) * mm});
            skLineSegment(sketch, "E248.right", {"start": v(-34.67, 14.14) * mm, "end": v(-34.67, 2.9) * mm});
            skPoint(sketch, "E248.middle", {"position": v(-35.96, 8.52) * mm});
            skEllipse(sketch, "E249", {"center": v(-28.03, 8.52) * mm, "majorRadius": 3.55 * mm, "minorRadius": 3.24 * mm, "majorAxis": v(0, 1)});
            skLineSegment(sketch, "E250.bottom", {"start": v(-4.73, 14.14) * mm, "end": v(-2.55, 14.14) * mm});
            skLineSegment(sketch, "E250.top", {"start": v(-4.73, 2.9) * mm, "end": v(-2.55, 2.9) * mm});
            skLineSegment(sketch, "E250.left", {"start": v(-4.73, 14.14) * mm, "end": v(-4.73, 2.9) * mm});
            skLineSegment(sketch, "E250.right", {"start": v(-2.55, 14.14) * mm, "end": v(-2.55, 2.9) * mm});
            skPoint(sketch, "E250.middle", {"position": v(-3.64, 8.52) * mm});
            skEllipse(sketch, "E251", {"center": v(-10.17, 8.52) * mm, "majorRadius": 3.27 * mm, "minorRadius": 2.06 * mm, "majorAxis": v(0, 1)});
            skLineSegment(sketch, "E252.bottom", {"start": v(-22.96, 14.14) * mm, "end": v(-20.24, 14.14) * mm});
            skLineSegment(sketch, "E252.top", {"start": v(-22.96, 2.9) * mm, "end": v(-20.24, 2.9) * mm});
            skLineSegment(sketch, "E252.left", {"start": v(-22.96, 14.14) * mm, "end": v(-22.96, 2.9) * mm});
            skLineSegment(sketch, "E252.right", {"start": v(-20.24, 14.14) * mm, "end": v(-20.24, 2.9) * mm});
            skPoint(sketch, "E252.middle", {"position": v(-21.6, 8.52) * mm});
            skLineSegment(sketch, "E253.bottom", {"start": v(-16.98, 14.14) * mm, "end": v(-14.8, 14.14) * mm});
            skLineSegment(sketch, "E253.top", {"start": v(-16.98, 2.9) * mm, "end": v(-14.8, 2.9) * mm});
            skLineSegment(sketch, "E253.left", {"start": v(-16.98, 14.14) * mm, "end": v(-16.98, 2.9) * mm});
            skLineSegment(sketch, "E253.right", {"start": v(-14.8, 14.14) * mm, "end": v(-14.8, 2.9) * mm});
            skPoint(sketch, "E253.middle", {"position": v(-15.89, 8.52) * mm});
            skLineSegment(sketch, "E254.MirrorCS", {"start": v(83.9, 14.14) * mm, "end": v(85.54, 14.14) * mm});
            skLineSegment(sketch, "E255.MirrorCS", {"start": v(16.98, 14.14) * mm, "end": v(14.8, 14.14) * mm});
            skLineSegment(sketch, "E256.MirrorCS", {"start": v(16.98, 2.9) * mm, "end": v(14.8, 2.9) * mm});
            skLineSegment(sketch, "E257.MirrorCS", {"start": v(37.26, 2.9) * mm, "end": v(34.67, 2.9) * mm});
            skLineSegment(sketch, "E258.MirrorCS", {"start": v(43.57, 14.14) * mm, "end": v(40.96, 14.14) * mm});
            skLineSegment(sketch, "E259.MirrorCS", {"start": v(43.57, 2.9) * mm, "end": v(40.96, 2.9) * mm});
            skLineSegment(sketch, "E260.MirrorCS", {"start": v(22.96, 2.9) * mm, "end": v(20.24, 2.9) * mm});
            skLineSegment(sketch, "E261.MirrorCS", {"start": v(69.48, 14.14) * mm, "end": v(66.22, 14.14) * mm});
            skLineSegment(sketch, "E262.MirrorCS", {"start": v(37.26, 14.14) * mm, "end": v(34.67, 14.14) * mm});
            skLineSegment(sketch, "E263.MirrorCS", {"start": v(4.73, 2.9) * mm, "end": v(2.55, 2.9) * mm});
            skLineSegment(sketch, "E264.MirrorCS", {"start": v(69.48, 2.9) * mm, "end": v(66.22, 2.9) * mm});
            skLineSegment(sketch, "E265.MirrorCS", {"start": v(83.9, 2.9) * mm, "end": v(85.54, 2.9) * mm});
            skLineSegment(sketch, "E266.MirrorCS", {"start": v(61.86, 2.9) * mm, "end": v(59.14, 2.9) * mm});
            skLineSegment(sketch, "E267.MirrorCS", {"start": v(22.96, 14.14) * mm, "end": v(20.24, 14.14) * mm});
            skLineSegment(sketch, "E268.MirrorCS", {"start": v(4.73, 14.14) * mm, "end": v(2.55, 14.14) * mm});
            skLineSegment(sketch, "E269.MirrorCS", {"start": v(61.86, 14.14) * mm, "end": v(59.14, 14.14) * mm});
            skEllipse(sketch, "E270.MirrorC", {"center": v(52.06, 8.52) * mm, "majorRadius": 4.63 * mm, "minorRadius": 2.73 * mm, "majorAxis": v(0, 1)});
            skPoint(sketch, "E271.MirrorP", {"position": v(21.6, 8.52) * mm});
            skLineSegment(sketch, "E272.MirrorCS", {"start": v(14.8, 14.14) * mm, "end": v(14.8, 2.9) * mm});
            skLineSegment(sketch, "E273.MirrorCS", {"start": v(22.96, 14.14) * mm, "end": v(22.96, 2.9) * mm});
            skLineSegment(sketch, "E274.MirrorCS", {"start": v(4.73, 14.14) * mm, "end": v(4.73, 2.9) * mm});
            skLineSegment(sketch, "E275.MirrorCS", {"start": v(83.9, 14.14) * mm, "end": v(83.9, 2.9) * mm});
            skPoint(sketch, "E276.MirrorP", {"position": v(15.89, 8.52) * mm});
            skLineSegment(sketch, "E277.MirrorCS", {"start": v(85.54, 14.14) * mm, "end": v(85.54, 2.9) * mm});
            skPoint(sketch, "E278.MirrorP", {"position": v(67.85, 8.52) * mm});
            skLineSegment(sketch, "E279.MirrorCS", {"start": v(43.57, 14.14) * mm, "end": v(43.57, 2.9) * mm});
            skLineSegment(sketch, "E280.MirrorCS", {"start": v(66.22, 14.14) * mm, "end": v(66.22, 2.9) * mm});
            skLineSegment(sketch, "E281.MirrorCS", {"start": v(59.14, 14.14) * mm, "end": v(59.14, 2.9) * mm});
            skPoint(sketch, "E282.MirrorP", {"position": v(84.73, 8.52) * mm});
            skLineSegment(sketch, "E283.MirrorCS", {"start": v(2.55, 14.14) * mm, "end": v(2.55, 2.9) * mm});
            skLineSegment(sketch, "E284.MirrorCS", {"start": v(61.86, 14.14) * mm, "end": v(61.86, 2.9) * mm});
            skLineSegment(sketch, "E285.MirrorCS", {"start": v(69.48, 14.14) * mm, "end": v(69.48, 2.9) * mm});
            skEllipse(sketch, "E286.MirrorC", {"center": v(10.17, 8.52) * mm, "majorRadius": 3.27 * mm, "minorRadius": 2.06 * mm, "majorAxis": v(0, 1)});
            skPoint(sketch, "E287.MirrorP", {"position": v(35.96, 8.52) * mm});
            skPoint(sketch, "E288.MirrorP", {"position": v(60.5, 8.52) * mm});
            skLineSegment(sketch, "E289.MirrorCS", {"start": v(16.98, 14.14) * mm, "end": v(16.98, 2.9) * mm});
            skLineSegment(sketch, "E290.MirrorCS", {"start": v(40.96, 14.14) * mm, "end": v(40.96, 2.9) * mm});
            skLineSegment(sketch, "E291.MirrorCS", {"start": v(34.67, 14.14) * mm, "end": v(34.67, 2.9) * mm});
            skPoint(sketch, "E292.MirrorP", {"position": v(42.27, 8.52) * mm});
            skCircle(sketch, "E293.MirrorC", {"center": v(77.1, 8.52) * mm, "radius": 3.7 * mm});
            skLineSegment(sketch, "E294.MirrorCS", {"start": v(37.26, 14.14) * mm, "end": v(37.26, 2.9) * mm});
            skLineSegment(sketch, "E295.MirrorCS", {"start": v(20.24, 14.14) * mm, "end": v(20.24, 2.9) * mm});
            skPoint(sketch, "E296.MirrorP", {"position": v(3.64, 8.52) * mm});
            skEllipse(sketch, "E297.MirrorC", {"center": v(28.03, 8.52) * mm, "majorRadius": 3.55 * mm, "minorRadius": 3.24 * mm, "majorAxis": v(0, 1)});
            skEllipse(sketch, "E298.MirrorC", {"center": v(-28.03, 8.52) * mm, "majorRadius": 3.55 * mm, "minorRadius": 3.24 * mm, "majorAxis": v(0, 1)});
            skEllipse(sketch, "E299.MirrorC", {"center": v(-10.17, 8.52) * mm, "majorRadius": 3.27 * mm, "minorRadius": 2.06 * mm, "majorAxis": v(0, 1)});
            skEllipse(sketch, "E300.MirrorC", {"center": v(28.03, 8.52) * mm, "majorRadius": 3.55 * mm, "minorRadius": 3.24 * mm, "majorAxis": v(0, 1)});
            skEllipse(sketch, "E301.MirrorC", {"center": v(10.17, 8.52) * mm, "majorRadius": 3.27 * mm, "minorRadius": 2.06 * mm, "majorAxis": v(0, 1)});
            skEllipse(sketch, "E302.MirrorC", {"center": v(-52.06, 8.52) * mm, "majorRadius": 4.63 * mm, "minorRadius": 2.73 * mm, "majorAxis": v(0, 1)});
            skEllipse(sketch, "E303.MirrorC", {"center": v(52.06, 8.52) * mm, "majorRadius": 4.63 * mm, "minorRadius": 2.73 * mm, "majorAxis": v(0, 1)});
            skEllipse(sketch, "E304.MirrorC", {"center": v(10.17, 8.52) * mm, "majorRadius": 3.27 * mm, "minorRadius": 2.06 * mm, "majorAxis": v(0, 1)});
            skEllipse(sketch, "E305.MirrorC", {"center": v(10.17, 8.52) * mm, "majorRadius": 3.27 * mm, "minorRadius": 2.06 * mm, "majorAxis": v(0, 1)});
            skEllipse(sketch, "E306.MirrorC", {"center": v(-10.17, 8.52) * mm, "majorRadius": 3.27 * mm, "minorRadius": 2.06 * mm, "majorAxis": v(0, 1)});
            skEllipse(sketch, "E307.MirrorC", {"center": v(-10.17, 8.52) * mm, "majorRadius": 3.27 * mm, "minorRadius": 2.06 * mm, "majorAxis": v(0, 1)});
            skEllipse(sketch, "E308.MirrorC", {"center": v(-28.03, 8.52) * mm, "majorRadius": 3.55 * mm, "minorRadius": 3.24 * mm, "majorAxis": v(0, 1)});
            skEllipse(sketch, "E309.MirrorC", {"center": v(28.03, 8.52) * mm, "majorRadius": 3.55 * mm, "minorRadius": 3.24 * mm, "majorAxis": v(0, 1)});
            skEllipse(sketch, "E310.MirrorC", {"center": v(-28.03, 8.52) * mm, "majorRadius": 3.55 * mm, "minorRadius": 3.24 * mm, "majorAxis": v(0, 1)});
            skEllipse(sketch, "E311.MirrorC", {"center": v(28.03, 8.52) * mm, "majorRadius": 3.55 * mm, "minorRadius": 3.24 * mm, "majorAxis": v(0, 1)});
            skLineSegment(sketch, "E312.MirrorCS", {"start": v(6.91, 19.72) * mm, "end": v(6.91, 16.63) * mm});
            skLineSegment(sketch, "E313.MirrorCS", {"start": v(55.55, 19.72) * mm, "end": v(55.55, 16.63) * mm});
            skEllipse(sketch, "E314.MirrorC", {"center": v(52.06, 8.52) * mm, "majorRadius": 4.63 * mm, "minorRadius": 2.73 * mm, "majorAxis": v(0, 1)});
            skEllipse(sketch, "E315.MirrorC", {"center": v(-52.06, 8.52) * mm, "majorRadius": 4.63 * mm, "minorRadius": 2.73 * mm, "majorAxis": v(0, 1)});
            skEllipse(sketch, "E316.MirrorC", {"center": v(52.06, 8.52) * mm, "majorRadius": 4.63 * mm, "minorRadius": 2.73 * mm, "majorAxis": v(0, 1)});
            skEllipse(sketch, "E317.MirrorC", {"center": v(-52.06, 8.52) * mm, "majorRadius": 4.63 * mm, "minorRadius": 2.73 * mm, "majorAxis": v(0, 1)});
            skLineSegment(sketch, "E318.MirrorCS", {"start": v(88.8, 8.52) * mm, "end": v(0, 8.52) * mm, "construction": true});
            skLineSegment(sketch, "E319.MirrorCS", {"start": v(55.55, 16.63) * mm, "end": v(6.91, 16.63) * mm});
            skLineSegment(sketch, "E320.MirrorCS", {"start": v(-55.55, 19.7) * mm, "end": v(-6.91, 19.7) * mm});
            skLineSegment(sketch, "E321.MirrorCS", {"start": v(55.55, 19.72) * mm, "end": v(6.91, 19.72) * mm});
            skLineSegment(sketch, "E322.MirrorCS", {"start": v(83.9, 87.61) * mm, "end": v(85.54, 87.61) * mm});
            skLineSegment(sketch, "E323.MirrorCS", {"start": v(4.73, 87.61) * mm, "end": v(2.55, 87.61) * mm});
            skLineSegment(sketch, "E324.MirrorCS", {"start": v(-43.57, 87.61) * mm, "end": v(-40.96, 87.61) * mm});
            skLineSegment(sketch, "E325.MirrorCS", {"start": v(16.98, 87.61) * mm, "end": v(14.8, 87.61) * mm});
            skLineSegment(sketch, "E326.MirrorCS", {"start": v(43.57, 87.61) * mm, "end": v(40.96, 87.61) * mm});
            skLineSegment(sketch, "E327.MirrorCS", {"start": v(22.96, 87.61) * mm, "end": v(20.24, 87.61) * mm});
            skLineSegment(sketch, "E328.MirrorCS", {"start": v(-16.98, 87.61) * mm, "end": v(-14.8, 87.61) * mm});
            skLineSegment(sketch, "E329.MirrorCS", {"start": v(-61.86, 87.61) * mm, "end": v(-59.14, 87.61) * mm});
            skLineSegment(sketch, "E330.MirrorCS", {"start": v(-69.48, 87.61) * mm, "end": v(-66.22, 87.61) * mm});
            skLineSegment(sketch, "E331.MirrorCS", {"start": v(61.86, 87.61) * mm, "end": v(59.14, 87.61) * mm});
            skLineSegment(sketch, "E332.MirrorCS", {"start": v(69.48, 87.61) * mm, "end": v(66.22, 87.61) * mm});
            skLineSegment(sketch, "E333.MirrorCS", {"start": v(37.26, 87.61) * mm, "end": v(34.67, 87.61) * mm});
            skLineSegment(sketch, "E334.MirrorCS", {"start": v(-4.73, 87.61) * mm, "end": v(-2.55, 87.61) * mm});
            skLineSegment(sketch, "E335.MirrorCS", {"start": v(-37.26, 87.61) * mm, "end": v(-34.67, 87.61) * mm});
            skLineSegment(sketch, "E336.MirrorCS", {"start": v(-22.96, 87.61) * mm, "end": v(-20.24, 87.61) * mm});
            skLineSegment(sketch, "E337.MirrorCS", {"start": v(-83.9, 87.61) * mm, "end": v(-85.54, 87.61) * mm});
            skLineSegment(sketch, "E338.MirrorCS", {"start": v(43.57, 87.61) * mm, "end": v(43.57, 98.85) * mm});
            skLineSegment(sketch, "E339.MirrorCS", {"start": v(-4.73, 87.61) * mm, "end": v(-4.73, 98.85) * mm});
            skEllipse(sketch, "E340.MirrorC", {"center": v(10.17, 93.23) * mm, "majorRadius": 3.27 * mm, "minorRadius": 2.06 * mm, "majorAxis": v(0, -1)});
            skPoint(sketch, "E341.MirrorP", {"position": v(-60.5, 93.23) * mm});
            skEllipse(sketch, "E342.MirrorC", {"center": v(-28.03, 93.23) * mm, "majorRadius": 3.55 * mm, "minorRadius": 3.24 * mm, "majorAxis": v(0, -1)});
            skLineSegment(sketch, "E343.MirrorCS", {"start": v(-83.9, 87.61) * mm, "end": v(-83.9, 98.85) * mm});
            skPoint(sketch, "E344.MirrorP", {"position": v(67.85, 93.23) * mm});
            skLineSegment(sketch, "E345.MirrorCS", {"start": v(-37.26, 98.85) * mm, "end": v(-34.67, 98.85) * mm});
            skLineSegment(sketch, "E346.MirrorCS", {"start": v(4.73, 98.85) * mm, "end": v(2.55, 98.85) * mm});
            skLineSegment(sketch, "E347.MirrorCS", {"start": v(61.86, 87.61) * mm, "end": v(61.86, 98.85) * mm});
            skPoint(sketch, "E348.MirrorP", {"position": v(21.6, 93.23) * mm});
            skLineSegment(sketch, "E349.MirrorCS", {"start": v(-22.96, 87.61) * mm, "end": v(-22.96, 98.85) * mm});
            skLineSegment(sketch, "E350.MirrorCS", {"start": v(-14.8, 87.61) * mm, "end": v(-14.8, 98.85) * mm});
            skLineSegment(sketch, "E351.MirrorCS", {"start": v(22.96, 98.85) * mm, "end": v(20.24, 98.85) * mm});
            skLineSegment(sketch, "E352.MirrorCS", {"start": v(-66.22, 87.61) * mm, "end": v(-66.22, 98.85) * mm});
            skLineSegment(sketch, "E353.MirrorCS", {"start": v(-85.54, 87.61) * mm, "end": v(-85.54, 98.85) * mm});
            skPoint(sketch, "E354.MirrorP", {"position": v(60.5, 93.23) * mm});
            skLineSegment(sketch, "E355.MirrorCS", {"start": v(16.98, 98.85) * mm, "end": v(14.8, 98.85) * mm});
            skLineSegment(sketch, "E356.MirrorCS", {"start": v(61.86, 98.85) * mm, "end": v(59.14, 98.85) * mm});
            skLineSegment(sketch, "E357.MirrorCS", {"start": v(85.54, 87.61) * mm, "end": v(85.54, 98.85) * mm});
            skLineSegment(sketch, "E358.MirrorCS", {"start": v(-22.96, 98.85) * mm, "end": v(-20.24, 98.85) * mm});
            skEllipse(sketch, "E359.MirrorC", {"center": v(52.06, 93.23) * mm, "majorRadius": 4.63 * mm, "minorRadius": 2.73 * mm, "majorAxis": v(0, -1)});
            skPoint(sketch, "E360.MirrorP", {"position": v(-84.73, 93.23) * mm});
            skLineSegment(sketch, "E361.MirrorCS", {"start": v(69.48, 98.85) * mm, "end": v(66.22, 98.85) * mm});
            skLineSegment(sketch, "E362.MirrorCS", {"start": v(20.24, 87.61) * mm, "end": v(20.24, 98.85) * mm});
            skLineSegment(sketch, "E363.MirrorCS", {"start": v(34.67, 87.61) * mm, "end": v(34.67, 98.85) * mm});
            skPoint(sketch, "E364.MirrorP", {"position": v(-15.89, 93.23) * mm});
            skCircle(sketch, "E365.MirrorC", {"center": v(77.1, 93.23) * mm, "radius": 3.7 * mm});
            skLineSegment(sketch, "E366.MirrorCS", {"start": v(59.14, 87.61) * mm, "end": v(59.14, 98.85) * mm});
            skLineSegment(sketch, "E367.MirrorCS", {"start": v(83.9, 98.85) * mm, "end": v(85.54, 98.85) * mm});
            skPoint(sketch, "E368.MirrorP", {"position": v(42.27, 93.23) * mm});
            skPoint(sketch, "E369.MirrorP", {"position": v(-35.96, 93.23) * mm});
            skPoint(sketch, "E370.MirrorP", {"position": v(3.64, 93.23) * mm});
            skPoint(sketch, "E371.MirrorP", {"position": v(15.89, 93.23) * mm});
            skPoint(sketch, "E372.MirrorP", {"position": v(35.96, 93.23) * mm});
            skLineSegment(sketch, "E373.MirrorCS", {"start": v(22.96, 87.61) * mm, "end": v(22.96, 98.85) * mm});
            skLineSegment(sketch, "E374.MirrorCS", {"start": v(-61.86, 98.85) * mm, "end": v(-59.14, 98.85) * mm});
            skLineSegment(sketch, "E375.MirrorCS", {"start": v(37.26, 87.61) * mm, "end": v(37.26, 98.85) * mm});
            skPoint(sketch, "E376.MirrorP", {"position": v(-42.27, 93.23) * mm});
            skLineSegment(sketch, "E377.MirrorCS", {"start": v(40.96, 87.61) * mm, "end": v(40.96, 98.85) * mm});
            skLineSegment(sketch, "E378.MirrorCS", {"start": v(16.98, 87.61) * mm, "end": v(16.98, 98.85) * mm});
            skLineSegment(sketch, "E379.MirrorCS", {"start": v(-61.86, 87.61) * mm, "end": v(-61.86, 98.85) * mm});
            skLineSegment(sketch, "E380.MirrorCS", {"start": v(-20.24, 87.61) * mm, "end": v(-20.24, 98.85) * mm});
            skLineSegment(sketch, "E381.MirrorCS", {"start": v(-34.67, 87.61) * mm, "end": v(-34.67, 98.85) * mm});
            skLineSegment(sketch, "E382.MirrorCS", {"start": v(-83.9, 98.85) * mm, "end": v(-85.54, 98.85) * mm});
            skLineSegment(sketch, "E383.MirrorCS", {"start": v(-2.55, 87.61) * mm, "end": v(-2.55, 98.85) * mm});
            skLineSegment(sketch, "E384.MirrorCS", {"start": v(-16.98, 98.85) * mm, "end": v(-14.8, 98.85) * mm});
            skLineSegment(sketch, "E385.MirrorCS", {"start": v(83.9, 87.61) * mm, "end": v(83.9, 98.85) * mm});
            skLineSegment(sketch, "E386.MirrorCS", {"start": v(4.73, 87.61) * mm, "end": v(4.73, 98.85) * mm});
            skLineSegment(sketch, "E387.MirrorCS", {"start": v(-59.14, 87.61) * mm, "end": v(-59.14, 98.85) * mm});
            skPoint(sketch, "E388.MirrorP", {"position": v(-21.6, 93.23) * mm});
            skEllipse(sketch, "E389.MirrorC", {"center": v(28.03, 93.23) * mm, "majorRadius": 3.55 * mm, "minorRadius": 3.24 * mm, "majorAxis": v(0, -1)});
            skLineSegment(sketch, "E390.MirrorCS", {"start": v(-43.57, 87.61) * mm, "end": v(-43.57, 98.85) * mm});
            skLineSegment(sketch, "E391.MirrorCS", {"start": v(2.55, 87.61) * mm, "end": v(2.55, 98.85) * mm});
            skLineSegment(sketch, "E392.MirrorCS", {"start": v(43.57, 98.85) * mm, "end": v(40.96, 98.85) * mm});
            skEllipse(sketch, "E393.MirrorC", {"center": v(-52.06, 93.23) * mm, "majorRadius": 4.63 * mm, "minorRadius": 2.73 * mm, "majorAxis": v(0, -1)});
            skLineSegment(sketch, "E394.MirrorCS", {"start": v(66.22, 87.61) * mm, "end": v(66.22, 98.85) * mm});
            skLineSegment(sketch, "E395.MirrorCS", {"start": v(69.48, 87.61) * mm, "end": v(69.48, 98.85) * mm});
            skLineSegment(sketch, "E396.MirrorCS", {"start": v(-69.48, 98.85) * mm, "end": v(-66.22, 98.85) * mm});
            skEllipse(sketch, "E397.MirrorC", {"center": v(-10.17, 93.23) * mm, "majorRadius": 3.27 * mm, "minorRadius": 2.06 * mm, "majorAxis": v(0, -1)});
            skLineSegment(sketch, "E398.MirrorCS", {"start": v(-43.57, 98.85) * mm, "end": v(-40.96, 98.85) * mm});
            skLineSegment(sketch, "E399.MirrorCS", {"start": v(37.26, 98.85) * mm, "end": v(34.67, 98.85) * mm});
            skLineSegment(sketch, "E400.MirrorCS", {"start": v(-37.26, 87.61) * mm, "end": v(-37.26, 98.85) * mm});
            skLineSegment(sketch, "E401.MirrorCS", {"start": v(14.8, 87.61) * mm, "end": v(14.8, 98.85) * mm});
            skPoint(sketch, "E402.MirrorP", {"position": v(-3.64, 93.23) * mm});
            skLineSegment(sketch, "E403.MirrorCS", {"start": v(-4.73, 98.85) * mm, "end": v(-2.55, 98.85) * mm});
            skCircle(sketch, "E404.MirrorC", {"center": v(-77.1, 93.23) * mm, "radius": 3.7 * mm});
            skPoint(sketch, "E405.MirrorP", {"position": v(-67.85, 93.23) * mm});
            skLineSegment(sketch, "E406.MirrorCS", {"start": v(-16.98, 87.61) * mm, "end": v(-16.98, 98.85) * mm});
            skPoint(sketch, "E407.MirrorP", {"position": v(84.73, 93.23) * mm});
            skLineSegment(sketch, "E408.MirrorCS", {"start": v(-69.48, 87.61) * mm, "end": v(-69.48, 98.85) * mm});
            skLineSegment(sketch, "E409.MirrorCS", {"start": v(-40.96, 87.61) * mm, "end": v(-40.96, 98.85) * mm});
            skEllipse(sketch, "E410.MirrorC", {"center": v(10.17, 93.23) * mm, "majorRadius": 3.27 * mm, "minorRadius": 2.06 * mm, "majorAxis": v(0, -1)});
            skEllipse(sketch, "E411.MirrorC", {"center": v(28.03, 93.23) * mm, "majorRadius": 3.55 * mm, "minorRadius": 3.24 * mm, "majorAxis": v(0, -1)});
            skEllipse(sketch, "E412.MirrorC", {"center": v(52.06, 93.23) * mm, "majorRadius": 4.63 * mm, "minorRadius": 2.73 * mm, "majorAxis": v(0, -1)});
            skEllipse(sketch, "E413.MirrorC", {"center": v(-28.03, 93.23) * mm, "majorRadius": 3.55 * mm, "minorRadius": 3.24 * mm, "majorAxis": v(0, -1)});
            skEllipse(sketch, "E414.MirrorC", {"center": v(-10.17, 93.23) * mm, "majorRadius": 3.27 * mm, "minorRadius": 2.06 * mm, "majorAxis": v(0, -1)});
            skEllipse(sketch, "E415.MirrorC", {"center": v(-52.06, 93.23) * mm, "majorRadius": 4.63 * mm, "minorRadius": 2.73 * mm, "majorAxis": v(0, -1)});
            skEllipse(sketch, "E416.MirrorC", {"center": v(10.17, 93.23) * mm, "majorRadius": 3.27 * mm, "minorRadius": 2.06 * mm, "majorAxis": v(0, -1)});
            skEllipse(sketch, "E417.MirrorC", {"center": v(-28.03, 93.23) * mm, "majorRadius": 3.55 * mm, "minorRadius": 3.24 * mm, "majorAxis": v(0, -1)});
            skEllipse(sketch, "E418.MirrorC", {"center": v(52.06, 93.23) * mm, "majorRadius": 4.63 * mm, "minorRadius": 2.73 * mm, "majorAxis": v(0, -1)});
            skEllipse(sketch, "E419.MirrorC", {"center": v(28.03, 93.23) * mm, "majorRadius": 3.55 * mm, "minorRadius": 3.24 * mm, "majorAxis": v(0, -1)});
            skEllipse(sketch, "E420.MirrorC", {"center": v(-10.17, 93.23) * mm, "majorRadius": 3.27 * mm, "minorRadius": 2.06 * mm, "majorAxis": v(0, -1)});
            skEllipse(sketch, "E421.MirrorC", {"center": v(-52.06, 93.23) * mm, "majorRadius": 4.63 * mm, "minorRadius": 2.73 * mm, "majorAxis": v(0, -1)});
            skEllipse(sketch, "E422.MirrorC", {"center": v(-28.03, 93.23) * mm, "majorRadius": 3.55 * mm, "minorRadius": 3.24 * mm, "majorAxis": v(0, -1)});
            skEllipse(sketch, "E423.MirrorC", {"center": v(-10.17, 93.23) * mm, "majorRadius": 3.27 * mm, "minorRadius": 2.06 * mm, "majorAxis": v(0, -1)});
            skEllipse(sketch, "E424.MirrorC", {"center": v(28.03, 93.23) * mm, "majorRadius": 3.55 * mm, "minorRadius": 3.24 * mm, "majorAxis": v(0, -1)});
            skEllipse(sketch, "E425.MirrorC", {"center": v(10.17, 93.23) * mm, "majorRadius": 3.27 * mm, "minorRadius": 2.06 * mm, "majorAxis": v(0, -1)});
            skEllipse(sketch, "E426.MirrorC", {"center": v(52.06, 93.23) * mm, "majorRadius": 4.63 * mm, "minorRadius": 2.73 * mm, "majorAxis": v(0, -1)});
            skEllipse(sketch, "E427.MirrorC", {"center": v(-52.06, 93.23) * mm, "majorRadius": 4.63 * mm, "minorRadius": 2.73 * mm, "majorAxis": v(0, -1)});
            skLineSegment(sketch, "E428", {"start": v(-87.13, 83.97) * mm, "end": v(-87.13, 74.95) * mm});
            skLineSegment(sketch, "E429", {"start": v(-87.13, 74.95) * mm, "end": v(-77.27, 78.94) * mm});
            skLineSegment(sketch, "E430", {"start": v(-77.27, 78.94) * mm, "end": v(-87.13, 83.97) * mm});
            skLineSegment(sketch, "E431", {"start": v(-75.03, 76.46) * mm, "end": v(-82.1, 74.53) * mm});
            skLineSegment(sketch, "E432", {"start": v(-82.1, 74.53) * mm, "end": v(-75.03, 68.43) * mm});
            skLineSegment(sketch, "E433", {"start": v(-75.03, 68.43) * mm, "end": v(-75.03, 76.46) * mm});
            skLineSegment(sketch, "E434", {"start": v(-87.13, 68.86) * mm, "end": v(-87.13, 61.52) * mm});
            skLineSegment(sketch, "E435", {"start": v(-87.13, 61.52) * mm, "end": v(-77.27, 67.4) * mm});
            skLineSegment(sketch, "E436", {"start": v(-77.27, 67.4) * mm, "end": v(-87.13, 68.86) * mm});
            skLineSegment(sketch, "E437", {"start": v(-75.03, 64.64) * mm, "end": v(-84.7, 58.88) * mm});
            skLineSegment(sketch, "E438", {"start": v(-84.7, 58.88) * mm, "end": v(-75.03, 57.44) * mm});
            skLineSegment(sketch, "E439", {"start": v(-75.03, 57.44) * mm, "end": v(-75.03, 64.64) * mm});
            skLineSegment(sketch, "E440", {"start": v(-86.66, 50.88) * mm, "end": v(-86.66, 55.92) * mm});
            skLineSegment(sketch, "E441", {"start": v(-86.66, 55.92) * mm, "end": v(-70.88, 50.88) * mm});
            skLineSegment(sketch, "E442.MirrorCS", {"start": v(-86.66, 50.88) * mm, "end": v(-86.66, 45.83) * mm});
            skLineSegment(sketch, "E443.MirrorCS", {"start": v(-86.66, 45.83) * mm, "end": v(-70.88, 50.88) * mm});
            skLineSegment(sketch, "E444.MirrorCS", {"start": v(-75.03, 44.3) * mm, "end": v(-75.03, 37.1) * mm});
            skLineSegment(sketch, "E445.MirrorCS", {"start": v(-77.27, 34.36) * mm, "end": v(-87.13, 32.89) * mm});
            skLineSegment(sketch, "E446.MirrorCS", {"start": v(-77.27, 22.81) * mm, "end": v(-87.13, 17.78) * mm});
            skLineSegment(sketch, "E447.MirrorCS", {"start": v(-75.03, 25.3) * mm, "end": v(-82.1, 27.22) * mm});
            skLineSegment(sketch, "E448.MirrorCS", {"start": v(-87.13, 26.8) * mm, "end": v(-77.27, 22.81) * mm});
            skLineSegment(sketch, "E449.MirrorCS", {"start": v(-84.7, 42.87) * mm, "end": v(-75.03, 44.3) * mm});
            skLineSegment(sketch, "E450.MirrorCS", {"start": v(-87.13, 40.23) * mm, "end": v(-77.27, 34.36) * mm});
            skLineSegment(sketch, "E451.MirrorCS", {"start": v(-75.03, 33.33) * mm, "end": v(-75.03, 25.3) * mm});
            skLineSegment(sketch, "E452.MirrorCS", {"start": v(-82.1, 27.22) * mm, "end": v(-75.03, 33.33) * mm});
            skLineSegment(sketch, "E453.MirrorCS", {"start": v(-87.13, 32.89) * mm, "end": v(-87.13, 40.23) * mm});
            skLineSegment(sketch, "E454.MirrorCS", {"start": v(-75.03, 37.1) * mm, "end": v(-84.7, 42.87) * mm});
            skLineSegment(sketch, "E455.MirrorCS", {"start": v(-87.13, 17.78) * mm, "end": v(-87.13, 26.8) * mm});
            skLineSegment(sketch, "E456.MirrorCS", {"start": v(86.66, 45.83) * mm, "end": v(70.88, 50.88) * mm});
            skLineSegment(sketch, "E457.MirrorCS", {"start": v(86.66, 55.92) * mm, "end": v(70.88, 50.88) * mm});
            skLineSegment(sketch, "E458.MirrorCS", {"start": v(86.66, 50.88) * mm, "end": v(86.66, 45.83) * mm});
            skLineSegment(sketch, "E459.MirrorCS", {"start": v(86.66, 50.88) * mm, "end": v(86.66, 55.92) * mm});
            skLineSegment(sketch, "E460.MirrorCS", {"start": v(75.03, 37.1) * mm, "end": v(84.7, 42.87) * mm});
            skLineSegment(sketch, "E461.MirrorCS", {"start": v(75.03, 25.3) * mm, "end": v(82.1, 27.22) * mm});
            skLineSegment(sketch, "E462.MirrorCS", {"start": v(87.13, 61.52) * mm, "end": v(77.27, 67.4) * mm});
            skLineSegment(sketch, "E463.MirrorCS", {"start": v(75.03, 33.33) * mm, "end": v(75.03, 25.3) * mm});
            skLineSegment(sketch, "E464.MirrorCS", {"start": v(82.1, 74.53) * mm, "end": v(75.03, 68.43) * mm});
            skLineSegment(sketch, "E465.MirrorCS", {"start": v(87.13, 26.8) * mm, "end": v(77.27, 22.81) * mm});
            skLineSegment(sketch, "E466.MirrorCS", {"start": v(75.03, 57.44) * mm, "end": v(75.03, 64.64) * mm});
            skLineSegment(sketch, "E467.MirrorCS", {"start": v(75.03, 68.43) * mm, "end": v(75.03, 76.46) * mm});
            skLineSegment(sketch, "E468.MirrorCS", {"start": v(77.27, 22.81) * mm, "end": v(87.13, 17.78) * mm});
            skLineSegment(sketch, "E469.MirrorCS", {"start": v(75.03, 44.3) * mm, "end": v(75.03, 37.1) * mm});
            skLineSegment(sketch, "E470.MirrorCS", {"start": v(87.13, 32.89) * mm, "end": v(87.13, 40.23) * mm});
            skLineSegment(sketch, "E471.MirrorCS", {"start": v(77.27, 78.94) * mm, "end": v(87.13, 83.97) * mm});
            skLineSegment(sketch, "E472.MirrorCS", {"start": v(87.13, 40.23) * mm, "end": v(77.27, 34.36) * mm});
            skLineSegment(sketch, "E473.MirrorCS", {"start": v(84.7, 58.88) * mm, "end": v(75.03, 57.44) * mm});
            skLineSegment(sketch, "E474.MirrorCS", {"start": v(77.27, 34.36) * mm, "end": v(87.13, 32.89) * mm});
            skLineSegment(sketch, "E475.MirrorCS", {"start": v(84.7, 42.87) * mm, "end": v(75.03, 44.3) * mm});
            skLineSegment(sketch, "E476.MirrorCS", {"start": v(82.1, 27.22) * mm, "end": v(75.03, 33.33) * mm});
            skLineSegment(sketch, "E477.MirrorCS", {"start": v(75.03, 76.46) * mm, "end": v(82.1, 74.53) * mm});
            skLineSegment(sketch, "E478.MirrorCS", {"start": v(75.03, 64.64) * mm, "end": v(84.7, 58.88) * mm});
            skLineSegment(sketch, "E479.MirrorCS", {"start": v(77.27, 67.4) * mm, "end": v(87.13, 68.86) * mm});
            skLineSegment(sketch, "E480.MirrorCS", {"start": v(87.13, 17.78) * mm, "end": v(87.13, 26.8) * mm});
            skLineSegment(sketch, "E481.MirrorCS", {"start": v(87.13, 83.97) * mm, "end": v(87.13, 74.95) * mm});
            skLineSegment(sketch, "E482.MirrorCS", {"start": v(87.13, 68.86) * mm, "end": v(87.13, 61.52) * mm});
            skLineSegment(sketch, "E483.MirrorCS", {"start": v(87.13, 74.95) * mm, "end": v(77.27, 78.94) * mm});
            skSolve(sketch);
        }
        {
            var Q0;
            Q0 = qSketchRegion(id + "F8", true);
            extrude(context, id + "F9", {"entities" : qUnion([Q0]), "operationType" : NewBodyOperationType.REMOVE, "oppositeDirection" : true, "depth" : 127 * mm, "offsetDistance" : 25.4 * mm});
        }
        {
            var Q0;
            Q0=makeQuery(id+"F4.opExtrude","SWEPT_FACE",FACE,{"disambiguationData":[OSD([sQuery(id+"F3.wireOp",EDGE,"E5.bottom")])]});
            var sketch = newSketch(context, id + "F10", { "sketchPlane" : qUnion([Q0])});
            skLineSegment(sketch, "E484", {"start": v(0, 101.6) * mm, "end": v(0, 111.13) * mm, "construction": true});
            skCircle(sketch, "E485", {"center": v(0, 106.36) * mm, "radius": 1.59 * mm});
            skLineSegment(sketch, "E486", {"start": v(0, 106.36) * mm, "end": v(-88.9, 106.36) * mm, "construction": true});
            skCircle(sketch, "E487", {"center": v(-16.51, 106.36) * mm, "radius": 1.59 * mm});
            skCircle(sketch, "E488", {"center": v(-33.02, 106.36) * mm, "radius": 1.59 * mm});
            skCircle(sketch, "E489", {"center": v(-49.53, 106.36) * mm, "radius": 1.59 * mm});
            skCircle(sketch, "E490", {"center": v(-66.04, 106.36) * mm, "radius": 1.59 * mm});
            skCircle(sketch, "E491", {"center": v(-82.55, 106.36) * mm, "radius": 1.59 * mm});
            skCircle(sketch, "E492.MirrorC", {"center": v(16.5, 106.36) * mm, "radius": 1.59 * mm});
            skCircle(sketch, "E493.MirrorC", {"center": v(33.02, 106.36) * mm, "radius": 1.59 * mm});
            skCircle(sketch, "E494.MirrorC", {"center": v(49.53, 106.36) * mm, "radius": 1.59 * mm});
            skCircle(sketch, "E495.MirrorC", {"center": v(66.04, 106.36) * mm, "radius": 1.59 * mm});
            skCircle(sketch, "E496.MirrorC", {"center": v(82.55, 106.36) * mm, "radius": 1.59 * mm});
            skLineSegment(sketch, "E497", {"start": v(0, 101.6) * mm, "end": v(0, 0) * mm, "construction": true});
            skPoint(sketch, "E498", {"position": v(0, 50.8) * mm});
            skLineSegment(sketch, "E499", {"start": v(0, 50.8) * mm, "end": v(-88.78, 50.8) * mm});
            skCircle(sketch, "E500.MirrorC", {"center": v(82.55, -4.76) * mm, "radius": 1.59 * mm});
            skCircle(sketch, "E501.MirrorC", {"center": v(66.04, -4.76) * mm, "radius": 1.59 * mm});
            skCircle(sketch, "E502.MirrorC", {"center": v(49.53, -4.76) * mm, "radius": 1.59 * mm});
            skCircle(sketch, "E503.MirrorC", {"center": v(33.02, -4.76) * mm, "radius": 1.59 * mm});
            skCircle(sketch, "E504.MirrorC", {"center": v(16.5, -4.76) * mm, "radius": 1.59 * mm});
            skCircle(sketch, "E505.MirrorC", {"center": v(0, -4.76) * mm, "radius": 1.59 * mm});
            skCircle(sketch, "E506.MirrorC", {"center": v(-16.51, -4.76) * mm, "radius": 1.59 * mm});
            skCircle(sketch, "E507.MirrorC", {"center": v(-33.02, -4.76) * mm, "radius": 1.59 * mm});
            skCircle(sketch, "E508.MirrorC", {"center": v(-49.53, -4.76) * mm, "radius": 1.59 * mm});
            skCircle(sketch, "E509.MirrorC", {"center": v(-66.04, -4.76) * mm, "radius": 1.59 * mm});
            skCircle(sketch, "E510.MirrorC", {"center": v(-82.55, -4.76) * mm, "radius": 1.59 * mm});
            skSolve(sketch);
        }
        {
            var Q0;
            Q0 = qSketchRegion(id + "F10", true);
            extrude(context, id + "F11", {"entities" : qUnion([Q0]), "operationType" : NewBodyOperationType.REMOVE, "oppositeDirection" : true, "depth" : 127 * mm, "offsetDistance" : 25.4 * mm});
        }
        {
            var Q0;
            Q0=makeQuery(id+"F1.opExtrude","SWEPT_FACE",FACE,{"disambiguationData":[OSD([sQuery(id+"F0.wireOp",EDGE,"E0.left")])]});
            var sketch = newSketch(context, id + "F12", { "sketchPlane" : qUnion([Q0])});
            skLineSegment(sketch, "E511", {"start": v(0, 101.6) * mm, "end": v(0, 0) * mm, "construction": true});
            skLineSegment(sketch, "E512", {"start": v(-38.1, 50.8) * mm, "end": v(38.1, 50.8) * mm, "construction": true});
            skLineSegment(sketch, "E513", {"start": v(-37.06, 92.03) * mm, "end": v(-30.53, 98.35) * mm});
            skLineSegment(sketch, "E514", {"start": v(-30.53, 98.35) * mm, "end": v(-30.53, 94.56) * mm});
            skLineSegment(sketch, "E515", {"start": v(-30.53, 94.56) * mm, "end": v(-24.56, 96.03) * mm});
            skLineSegment(sketch, "E516", {"start": v(-24.56, 96.03) * mm, "end": v(-29.12, 91.54) * mm});
            skLineSegment(sketch, "E517", {"start": v(-29.12, 91.54) * mm, "end": v(-27.35, 89.73) * mm});
            skLineSegment(sketch, "E518", {"start": v(-27.35, 89.73) * mm, "end": v(-22.31, 93.93) * mm});
            skLineSegment(sketch, "E519", {"start": v(-22.31, 93.93) * mm, "end": v(-24.45, 88.22) * mm});
            skLineSegment(sketch, "E520", {"start": v(-24.45, 88.22) * mm, "end": v(-20.23, 88.22) * mm});
            skLineSegment(sketch, "E521", {"start": v(-20.23, 88.22) * mm, "end": v(-26.8, 81.36) * mm});
            skLineSegment(sketch, "E522", {"start": v(-26.8, 81.36) * mm, "end": v(-27.44, 85.36) * mm});
            skLineSegment(sketch, "E523", {"start": v(-27.44, 85.36) * mm, "end": v(-33.12, 83.75) * mm});
            skLineSegment(sketch, "E524", {"start": v(-33.12, 83.75) * mm, "end": v(-28.21, 89.08) * mm});
            skLineSegment(sketch, "E525", {"start": v(-28.21, 89.08) * mm, "end": v(-29.85, 90.59) * mm});
            skLineSegment(sketch, "E526", {"start": v(-29.85, 90.59) * mm, "end": v(-34.82, 85.19) * mm});
            skLineSegment(sketch, "E527", {"start": v(-34.82, 85.19) * mm, "end": v(-33.2, 91.9) * mm});
            skLineSegment(sketch, "E528", {"start": v(-33.2, 91.9) * mm, "end": v(-37.06, 92.03) * mm});
            skPoint(sketch, "E529", {"position": v(0, 76.57) * mm});
            skPoint(sketch, "E530", {"position": v(0, 50.8) * mm});
            skPoint(sketch, "E531", {"position": v(-19.05, 76.57) * mm});
            skLineSegment(sketch, "E532", {"start": v(-19.05, 76.57) * mm, "end": v(-19.05, 50.8) * mm, "construction": true});
            skLineSegment(sketch, "E533.0.1.0", {"start": v(-33.12, 64.19) * mm, "end": v(-28.21, 69.52) * mm});
            skLineSegment(sketch, "E533.0.1.1", {"start": v(-24.56, 76.47) * mm, "end": v(-29.12, 71.98) * mm});
            skLineSegment(sketch, "E533.0.1.2", {"start": v(-22.31, 74.37) * mm, "end": v(-24.45, 68.66) * mm});
            skLineSegment(sketch, "E533.0.1.3", {"start": v(-20.23, 68.66) * mm, "end": v(-26.8, 61.8) * mm});
            skLineSegment(sketch, "E533.0.1.4", {"start": v(-27.35, 70.18) * mm, "end": v(-22.31, 74.37) * mm});
            skLineSegment(sketch, "E533.0.1.5", {"start": v(-29.85, 71.03) * mm, "end": v(-34.82, 65.63) * mm});
            skLineSegment(sketch, "E533.0.1.6", {"start": v(-37.06, 72.47) * mm, "end": v(-30.53, 78.8) * mm});
            skLineSegment(sketch, "E533.0.1.7", {"start": v(-27.44, 65.8) * mm, "end": v(-33.12, 64.19) * mm});
            skLineSegment(sketch, "E533.0.1.8", {"start": v(-34.82, 65.63) * mm, "end": v(-33.2, 72.33) * mm});
            skLineSegment(sketch, "E533.0.1.9", {"start": v(-30.53, 75) * mm, "end": v(-24.56, 76.47) * mm});
            skLineSegment(sketch, "E533.0.1.10", {"start": v(-24.45, 68.66) * mm, "end": v(-20.23, 68.66) * mm});
            skLineSegment(sketch, "E533.0.1.11", {"start": v(-33.2, 72.33) * mm, "end": v(-37.06, 72.47) * mm});
            skLineSegment(sketch, "E533.0.1.12", {"start": v(-26.8, 61.8) * mm, "end": v(-27.44, 65.8) * mm});
            skLineSegment(sketch, "E533.0.1.13", {"start": v(-29.12, 71.98) * mm, "end": v(-27.35, 70.18) * mm});
            skLineSegment(sketch, "E533.0.1.14", {"start": v(-30.53, 78.8) * mm, "end": v(-30.53, 75) * mm});
            skLineSegment(sketch, "E533.0.1.15", {"start": v(-28.21, 69.52) * mm, "end": v(-29.85, 71.03) * mm});
            skLineSegment(sketch, "E533.0.2.0", {"start": v(-33.12, 44.63) * mm, "end": v(-28.21, 49.97) * mm});
            skLineSegment(sketch, "E533.0.2.1", {"start": v(-24.56, 56.92) * mm, "end": v(-29.12, 52.42) * mm});
            skLineSegment(sketch, "E533.0.2.2", {"start": v(-22.31, 54.81) * mm, "end": v(-24.45, 49.1) * mm});
            skLineSegment(sketch, "E533.0.2.3", {"start": v(-20.23, 49.1) * mm, "end": v(-26.8, 42.24) * mm});
            skLineSegment(sketch, "E533.0.2.4", {"start": v(-27.35, 50.62) * mm, "end": v(-22.31, 54.81) * mm});
            skLineSegment(sketch, "E533.0.2.5", {"start": v(-29.85, 51.47) * mm, "end": v(-34.82, 46.07) * mm});
            skLineSegment(sketch, "E533.0.2.6", {"start": v(-37.06, 52.91) * mm, "end": v(-30.53, 59.23) * mm});
            skLineSegment(sketch, "E533.0.2.7", {"start": v(-27.44, 46.25) * mm, "end": v(-33.12, 44.63) * mm});
            skLineSegment(sketch, "E533.0.2.8", {"start": v(-34.82, 46.07) * mm, "end": v(-33.2, 52.77) * mm});
            skLineSegment(sketch, "E533.0.2.9", {"start": v(-30.53, 55.44) * mm, "end": v(-24.56, 56.92) * mm});
            skLineSegment(sketch, "E533.0.2.10", {"start": v(-24.45, 49.1) * mm, "end": v(-20.23, 49.1) * mm});
            skLineSegment(sketch, "E533.0.2.11", {"start": v(-33.2, 52.77) * mm, "end": v(-37.06, 52.91) * mm});
            skLineSegment(sketch, "E533.0.2.12", {"start": v(-26.8, 42.24) * mm, "end": v(-27.44, 46.25) * mm});
            skLineSegment(sketch, "E533.0.2.13", {"start": v(-29.12, 52.42) * mm, "end": v(-27.35, 50.62) * mm});
            skLineSegment(sketch, "E533.0.2.14", {"start": v(-30.53, 59.23) * mm, "end": v(-30.53, 55.44) * mm});
            skLineSegment(sketch, "E533.0.2.15", {"start": v(-28.21, 49.97) * mm, "end": v(-29.85, 51.47) * mm});
            skLineSegment(sketch, "E533.0.3.0", {"start": v(-33.12, 25.07) * mm, "end": v(-28.21, 30.4) * mm});
            skLineSegment(sketch, "E533.0.3.1", {"start": v(-24.56, 37.36) * mm, "end": v(-29.12, 32.87) * mm});
            skLineSegment(sketch, "E533.0.3.2", {"start": v(-22.31, 35.25) * mm, "end": v(-24.45, 29.54) * mm});
            skLineSegment(sketch, "E533.0.3.3", {"start": v(-20.23, 29.54) * mm, "end": v(-26.8, 22.69) * mm});
            skLineSegment(sketch, "E533.0.3.4", {"start": v(-27.35, 31.06) * mm, "end": v(-22.31, 35.25) * mm});
            skLineSegment(sketch, "E533.0.3.5", {"start": v(-29.85, 31.92) * mm, "end": v(-34.82, 26.52) * mm});
            skLineSegment(sketch, "E533.0.3.6", {"start": v(-37.06, 33.36) * mm, "end": v(-30.53, 39.67) * mm});
            skLineSegment(sketch, "E533.0.3.7", {"start": v(-27.44, 26.69) * mm, "end": v(-33.12, 25.07) * mm});
            skLineSegment(sketch, "E533.0.3.8", {"start": v(-34.82, 26.52) * mm, "end": v(-33.2, 33.22) * mm});
            skLineSegment(sketch, "E533.0.3.9", {"start": v(-30.53, 35.88) * mm, "end": v(-24.56, 37.36) * mm});
            skLineSegment(sketch, "E533.0.3.10", {"start": v(-24.45, 29.54) * mm, "end": v(-20.23, 29.54) * mm});
            skLineSegment(sketch, "E533.0.3.11", {"start": v(-33.2, 33.22) * mm, "end": v(-37.06, 33.36) * mm});
            skLineSegment(sketch, "E533.0.3.12", {"start": v(-26.8, 22.69) * mm, "end": v(-27.44, 26.69) * mm});
            skLineSegment(sketch, "E533.0.3.13", {"start": v(-29.12, 32.87) * mm, "end": v(-27.35, 31.06) * mm});
            skLineSegment(sketch, "E533.0.3.14", {"start": v(-30.53, 39.67) * mm, "end": v(-30.53, 35.88) * mm});
            skLineSegment(sketch, "E533.0.3.15", {"start": v(-28.21, 30.4) * mm, "end": v(-29.85, 31.92) * mm});
            skLineSegment(sketch, "E533.1.0.0", {"start": v(-14.07, 83.75) * mm, "end": v(-9.16, 89.08) * mm});
            skLineSegment(sketch, "E533.1.0.1", {"start": v(-5.5, 96.03) * mm, "end": v(-10.07, 91.54) * mm});
            skLineSegment(sketch, "E533.1.0.2", {"start": v(-3.26, 93.93) * mm, "end": v(-5.4, 88.22) * mm});
            skLineSegment(sketch, "E533.1.0.3", {"start": v(-1.18, 88.22) * mm, "end": v(-7.76, 81.36) * mm});
            skLineSegment(sketch, "E533.1.0.4", {"start": v(-8.3, 89.73) * mm, "end": v(-3.26, 93.93) * mm});
            skLineSegment(sketch, "E533.1.0.5", {"start": v(-10.8, 90.59) * mm, "end": v(-15.77, 85.19) * mm});
            skLineSegment(sketch, "E533.1.0.6", {"start": v(-18, 92.03) * mm, "end": v(-11.48, 98.35) * mm});
            skLineSegment(sketch, "E533.1.0.7", {"start": v(-8.39, 85.36) * mm, "end": v(-14.07, 83.75) * mm});
            skLineSegment(sketch, "E533.1.0.8", {"start": v(-15.77, 85.19) * mm, "end": v(-14.14, 91.9) * mm});
            skLineSegment(sketch, "E533.1.0.9", {"start": v(-11.48, 94.56) * mm, "end": v(-5.5, 96.03) * mm});
            skLineSegment(sketch, "E533.1.0.10", {"start": v(-5.4, 88.22) * mm, "end": v(-1.18, 88.22) * mm});
            skLineSegment(sketch, "E533.1.0.11", {"start": v(-14.14, 91.9) * mm, "end": v(-18, 92.03) * mm});
            skLineSegment(sketch, "E533.1.0.12", {"start": v(-7.76, 81.36) * mm, "end": v(-8.39, 85.36) * mm});
            skLineSegment(sketch, "E533.1.0.13", {"start": v(-10.07, 91.54) * mm, "end": v(-8.3, 89.73) * mm});
            skLineSegment(sketch, "E533.1.0.14", {"start": v(-11.48, 98.35) * mm, "end": v(-11.48, 94.56) * mm});
            skLineSegment(sketch, "E533.1.0.15", {"start": v(-9.16, 89.08) * mm, "end": v(-10.8, 90.59) * mm});
            skLineSegment(sketch, "E533.1.1.0", {"start": v(-14.07, 64.19) * mm, "end": v(-9.16, 69.52) * mm});
            skLineSegment(sketch, "E533.1.1.1", {"start": v(-5.5, 76.47) * mm, "end": v(-10.07, 71.98) * mm});
            skLineSegment(sketch, "E533.1.1.2", {"start": v(-3.26, 74.37) * mm, "end": v(-5.4, 68.66) * mm});
            skLineSegment(sketch, "E533.1.1.3", {"start": v(-1.18, 68.66) * mm, "end": v(-7.76, 61.8) * mm});
            skLineSegment(sketch, "E533.1.1.4", {"start": v(-8.3, 70.18) * mm, "end": v(-3.26, 74.37) * mm});
            skLineSegment(sketch, "E533.1.1.5", {"start": v(-10.8, 71.03) * mm, "end": v(-15.77, 65.63) * mm});
            skLineSegment(sketch, "E533.1.1.6", {"start": v(-18, 72.47) * mm, "end": v(-11.48, 78.8) * mm});
            skLineSegment(sketch, "E533.1.1.7", {"start": v(-8.39, 65.8) * mm, "end": v(-14.07, 64.19) * mm});
            skLineSegment(sketch, "E533.1.1.8", {"start": v(-15.77, 65.63) * mm, "end": v(-14.14, 72.33) * mm});
            skLineSegment(sketch, "E533.1.1.9", {"start": v(-11.48, 75) * mm, "end": v(-5.5, 76.47) * mm});
            skLineSegment(sketch, "E533.1.1.10", {"start": v(-5.4, 68.66) * mm, "end": v(-1.18, 68.66) * mm});
            skLineSegment(sketch, "E533.1.1.11", {"start": v(-14.14, 72.33) * mm, "end": v(-18, 72.47) * mm});
            skLineSegment(sketch, "E533.1.1.12", {"start": v(-7.76, 61.8) * mm, "end": v(-8.39, 65.8) * mm});
            skLineSegment(sketch, "E533.1.1.13", {"start": v(-10.07, 71.98) * mm, "end": v(-8.3, 70.18) * mm});
            skLineSegment(sketch, "E533.1.1.14", {"start": v(-11.48, 78.8) * mm, "end": v(-11.48, 75) * mm});
            skLineSegment(sketch, "E533.1.1.15", {"start": v(-9.16, 69.52) * mm, "end": v(-10.8, 71.03) * mm});
            skLineSegment(sketch, "E533.1.2.0", {"start": v(-14.07, 44.63) * mm, "end": v(-9.16, 49.97) * mm});
            skLineSegment(sketch, "E533.1.2.1", {"start": v(-5.5, 56.92) * mm, "end": v(-10.07, 52.42) * mm});
            skLineSegment(sketch, "E533.1.2.2", {"start": v(-3.26, 54.81) * mm, "end": v(-5.4, 49.1) * mm});
            skLineSegment(sketch, "E533.1.2.3", {"start": v(-1.18, 49.1) * mm, "end": v(-7.76, 42.24) * mm});
            skLineSegment(sketch, "E533.1.2.4", {"start": v(-8.3, 50.62) * mm, "end": v(-3.26, 54.81) * mm});
            skLineSegment(sketch, "E533.1.2.5", {"start": v(-10.8, 51.47) * mm, "end": v(-15.77, 46.07) * mm});
            skLineSegment(sketch, "E533.1.2.6", {"start": v(-18, 52.91) * mm, "end": v(-11.48, 59.23) * mm});
            skLineSegment(sketch, "E533.1.2.7", {"start": v(-8.39, 46.25) * mm, "end": v(-14.07, 44.63) * mm});
            skLineSegment(sketch, "E533.1.2.8", {"start": v(-15.77, 46.07) * mm, "end": v(-14.14, 52.77) * mm});
            skLineSegment(sketch, "E533.1.2.9", {"start": v(-11.48, 55.44) * mm, "end": v(-5.5, 56.92) * mm});
            skLineSegment(sketch, "E533.1.2.10", {"start": v(-5.4, 49.1) * mm, "end": v(-1.18, 49.1) * mm});
            skLineSegment(sketch, "E533.1.2.11", {"start": v(-14.14, 52.77) * mm, "end": v(-18, 52.91) * mm});
            skLineSegment(sketch, "E533.1.2.12", {"start": v(-7.76, 42.24) * mm, "end": v(-8.39, 46.25) * mm});
            skLineSegment(sketch, "E533.1.2.13", {"start": v(-10.07, 52.42) * mm, "end": v(-8.3, 50.62) * mm});
            skLineSegment(sketch, "E533.1.2.14", {"start": v(-11.48, 59.23) * mm, "end": v(-11.48, 55.44) * mm});
            skLineSegment(sketch, "E533.1.2.15", {"start": v(-9.16, 49.97) * mm, "end": v(-10.8, 51.47) * mm});
            skLineSegment(sketch, "E533.1.3.0", {"start": v(-14.07, 25.07) * mm, "end": v(-9.16, 30.4) * mm});
            skLineSegment(sketch, "E533.1.3.1", {"start": v(-5.5, 37.36) * mm, "end": v(-10.07, 32.87) * mm});
            skLineSegment(sketch, "E533.1.3.2", {"start": v(-3.26, 35.25) * mm, "end": v(-5.4, 29.54) * mm});
            skLineSegment(sketch, "E533.1.3.3", {"start": v(-1.18, 29.54) * mm, "end": v(-7.76, 22.69) * mm});
            skLineSegment(sketch, "E533.1.3.4", {"start": v(-8.3, 31.06) * mm, "end": v(-3.26, 35.25) * mm});
            skLineSegment(sketch, "E533.1.3.5", {"start": v(-10.8, 31.92) * mm, "end": v(-15.77, 26.52) * mm});
            skLineSegment(sketch, "E533.1.3.6", {"start": v(-18, 33.36) * mm, "end": v(-11.48, 39.67) * mm});
            skLineSegment(sketch, "E533.1.3.7", {"start": v(-8.39, 26.69) * mm, "end": v(-14.07, 25.07) * mm});
            skLineSegment(sketch, "E533.1.3.8", {"start": v(-15.77, 26.52) * mm, "end": v(-14.14, 33.22) * mm});
            skLineSegment(sketch, "E533.1.3.9", {"start": v(-11.48, 35.88) * mm, "end": v(-5.5, 37.36) * mm});
            skLineSegment(sketch, "E533.1.3.10", {"start": v(-5.4, 29.54) * mm, "end": v(-1.18, 29.54) * mm});
            skLineSegment(sketch, "E533.1.3.11", {"start": v(-14.14, 33.22) * mm, "end": v(-18, 33.36) * mm});
            skLineSegment(sketch, "E533.1.3.12", {"start": v(-7.76, 22.69) * mm, "end": v(-8.39, 26.69) * mm});
            skLineSegment(sketch, "E533.1.3.13", {"start": v(-10.07, 32.87) * mm, "end": v(-8.3, 31.06) * mm});
            skLineSegment(sketch, "E533.1.3.14", {"start": v(-11.48, 39.67) * mm, "end": v(-11.48, 35.88) * mm});
            skLineSegment(sketch, "E533.1.3.15", {"start": v(-9.16, 30.4) * mm, "end": v(-10.8, 31.92) * mm});
            skLineSegment(sketch, "E533.2.0.0", {"start": v(4.98, 83.75) * mm, "end": v(9.89, 89.08) * mm});
            skLineSegment(sketch, "E533.2.0.1", {"start": v(13.54, 96.03) * mm, "end": v(8.98, 91.54) * mm});
            skLineSegment(sketch, "E533.2.0.2", {"start": v(15.79, 93.93) * mm, "end": v(13.65, 88.22) * mm});
            skLineSegment(sketch, "E533.2.0.3", {"start": v(17.87, 88.22) * mm, "end": v(11.3, 81.36) * mm});
            skLineSegment(sketch, "E533.2.0.4", {"start": v(10.75, 89.73) * mm, "end": v(15.79, 93.93) * mm});
            skLineSegment(sketch, "E533.2.0.5", {"start": v(8.25, 90.59) * mm, "end": v(3.28, 85.19) * mm});
            skLineSegment(sketch, "E533.2.0.6", {"start": v(1.04, 92.03) * mm, "end": v(7.57, 98.35) * mm});
            skLineSegment(sketch, "E533.2.0.7", {"start": v(10.66, 85.36) * mm, "end": v(4.98, 83.75) * mm});
            skLineSegment(sketch, "E533.2.0.8", {"start": v(3.28, 85.19) * mm, "end": v(4.9, 91.9) * mm});
            skLineSegment(sketch, "E533.2.0.9", {"start": v(7.57, 94.56) * mm, "end": v(13.54, 96.03) * mm});
            skLineSegment(sketch, "E533.2.0.10", {"start": v(13.65, 88.22) * mm, "end": v(17.87, 88.22) * mm});
            skLineSegment(sketch, "E533.2.0.11", {"start": v(4.9, 91.9) * mm, "end": v(1.04, 92.03) * mm});
            skLineSegment(sketch, "E533.2.0.12", {"start": v(11.3, 81.36) * mm, "end": v(10.66, 85.36) * mm});
            skLineSegment(sketch, "E533.2.0.13", {"start": v(8.98, 91.54) * mm, "end": v(10.75, 89.73) * mm});
            skLineSegment(sketch, "E533.2.0.14", {"start": v(7.57, 98.35) * mm, "end": v(7.57, 94.56) * mm});
            skLineSegment(sketch, "E533.2.0.15", {"start": v(9.89, 89.08) * mm, "end": v(8.25, 90.59) * mm});
            skLineSegment(sketch, "E533.2.1.0", {"start": v(4.98, 64.19) * mm, "end": v(9.89, 69.52) * mm});
            skLineSegment(sketch, "E533.2.1.1", {"start": v(13.54, 76.47) * mm, "end": v(8.98, 71.98) * mm});
            skLineSegment(sketch, "E533.2.1.2", {"start": v(15.79, 74.37) * mm, "end": v(13.65, 68.66) * mm});
            skLineSegment(sketch, "E533.2.1.3", {"start": v(17.87, 68.66) * mm, "end": v(11.3, 61.8) * mm});
            skLineSegment(sketch, "E533.2.1.4", {"start": v(10.75, 70.18) * mm, "end": v(15.79, 74.37) * mm});
            skLineSegment(sketch, "E533.2.1.5", {"start": v(8.25, 71.03) * mm, "end": v(3.28, 65.63) * mm});
            skLineSegment(sketch, "E533.2.1.6", {"start": v(1.04, 72.47) * mm, "end": v(7.57, 78.8) * mm});
            skLineSegment(sketch, "E533.2.1.7", {"start": v(10.66, 65.8) * mm, "end": v(4.98, 64.19) * mm});
            skLineSegment(sketch, "E533.2.1.8", {"start": v(3.28, 65.63) * mm, "end": v(4.9, 72.33) * mm});
            skLineSegment(sketch, "E533.2.1.9", {"start": v(7.57, 75) * mm, "end": v(13.54, 76.47) * mm});
            skLineSegment(sketch, "E533.2.1.10", {"start": v(13.65, 68.66) * mm, "end": v(17.87, 68.66) * mm});
            skLineSegment(sketch, "E533.2.1.11", {"start": v(4.9, 72.33) * mm, "end": v(1.04, 72.47) * mm});
            skLineSegment(sketch, "E533.2.1.12", {"start": v(11.3, 61.8) * mm, "end": v(10.66, 65.8) * mm});
            skLineSegment(sketch, "E533.2.1.13", {"start": v(8.98, 71.98) * mm, "end": v(10.75, 70.18) * mm});
            skLineSegment(sketch, "E533.2.1.14", {"start": v(7.57, 78.8) * mm, "end": v(7.57, 75) * mm});
            skLineSegment(sketch, "E533.2.1.15", {"start": v(9.89, 69.52) * mm, "end": v(8.25, 71.03) * mm});
            skLineSegment(sketch, "E533.2.2.0", {"start": v(4.98, 44.63) * mm, "end": v(9.89, 49.97) * mm});
            skLineSegment(sketch, "E533.2.2.1", {"start": v(13.54, 56.92) * mm, "end": v(8.98, 52.42) * mm});
            skLineSegment(sketch, "E533.2.2.2", {"start": v(15.79, 54.81) * mm, "end": v(13.65, 49.1) * mm});
            skLineSegment(sketch, "E533.2.2.3", {"start": v(17.87, 49.1) * mm, "end": v(11.3, 42.24) * mm});
            skLineSegment(sketch, "E533.2.2.4", {"start": v(10.75, 50.62) * mm, "end": v(15.79, 54.81) * mm});
            skLineSegment(sketch, "E533.2.2.5", {"start": v(8.25, 51.47) * mm, "end": v(3.28, 46.07) * mm});
            skLineSegment(sketch, "E533.2.2.6", {"start": v(1.04, 52.91) * mm, "end": v(7.57, 59.23) * mm});
            skLineSegment(sketch, "E533.2.2.7", {"start": v(10.66, 46.25) * mm, "end": v(4.98, 44.63) * mm});
            skLineSegment(sketch, "E533.2.2.8", {"start": v(3.28, 46.07) * mm, "end": v(4.9, 52.77) * mm});
            skLineSegment(sketch, "E533.2.2.9", {"start": v(7.57, 55.44) * mm, "end": v(13.54, 56.92) * mm});
            skLineSegment(sketch, "E533.2.2.10", {"start": v(13.65, 49.1) * mm, "end": v(17.87, 49.1) * mm});
            skLineSegment(sketch, "E533.2.2.11", {"start": v(4.9, 52.77) * mm, "end": v(1.04, 52.91) * mm});
            skLineSegment(sketch, "E533.2.2.12", {"start": v(11.3, 42.24) * mm, "end": v(10.66, 46.25) * mm});
            skLineSegment(sketch, "E533.2.2.13", {"start": v(8.98, 52.42) * mm, "end": v(10.75, 50.62) * mm});
            skLineSegment(sketch, "E533.2.2.14", {"start": v(7.57, 59.23) * mm, "end": v(7.57, 55.44) * mm});
            skLineSegment(sketch, "E533.2.2.15", {"start": v(9.89, 49.97) * mm, "end": v(8.25, 51.47) * mm});
            skLineSegment(sketch, "E533.2.3.0", {"start": v(4.98, 25.07) * mm, "end": v(9.89, 30.4) * mm});
            skLineSegment(sketch, "E533.2.3.1", {"start": v(13.54, 37.36) * mm, "end": v(8.98, 32.87) * mm});
            skLineSegment(sketch, "E533.2.3.2", {"start": v(15.79, 35.25) * mm, "end": v(13.65, 29.54) * mm});
            skLineSegment(sketch, "E533.2.3.3", {"start": v(17.87, 29.54) * mm, "end": v(11.3, 22.69) * mm});
            skLineSegment(sketch, "E533.2.3.4", {"start": v(10.75, 31.06) * mm, "end": v(15.79, 35.25) * mm});
            skLineSegment(sketch, "E533.2.3.5", {"start": v(8.25, 31.92) * mm, "end": v(3.28, 26.52) * mm});
            skLineSegment(sketch, "E533.2.3.6", {"start": v(1.04, 33.36) * mm, "end": v(7.57, 39.67) * mm});
            skLineSegment(sketch, "E533.2.3.7", {"start": v(10.66, 26.69) * mm, "end": v(4.98, 25.07) * mm});
            skLineSegment(sketch, "E533.2.3.8", {"start": v(3.28, 26.52) * mm, "end": v(4.9, 33.22) * mm});
            skLineSegment(sketch, "E533.2.3.9", {"start": v(7.57, 35.88) * mm, "end": v(13.54, 37.36) * mm});
            skLineSegment(sketch, "E533.2.3.10", {"start": v(13.65, 29.54) * mm, "end": v(17.87, 29.54) * mm});
            skLineSegment(sketch, "E533.2.3.11", {"start": v(4.9, 33.22) * mm, "end": v(1.04, 33.36) * mm});
            skLineSegment(sketch, "E533.2.3.12", {"start": v(11.3, 22.69) * mm, "end": v(10.66, 26.69) * mm});
            skLineSegment(sketch, "E533.2.3.13", {"start": v(8.98, 32.87) * mm, "end": v(10.75, 31.06) * mm});
            skLineSegment(sketch, "E533.2.3.14", {"start": v(7.57, 39.67) * mm, "end": v(7.57, 35.88) * mm});
            skLineSegment(sketch, "E533.2.3.15", {"start": v(9.89, 30.4) * mm, "end": v(8.25, 31.92) * mm});
            skLineSegment(sketch, "E533.direction1", {"start": v(-34.82, 85.19) * mm, "end": v(-15.77, 85.19) * mm, "construction": true});
            skLineSegment(sketch, "E533.direction2", {"start": v(-34.82, 85.19) * mm, "end": v(-34.82, 65.63) * mm, "construction": true});
            skLineSegment(sketch, "E534.0.3.0", {"start": v(24.03, 83.75) * mm, "end": v(28.94, 89.08) * mm});
            skLineSegment(sketch, "E534.3.3.0", {"start": v(32.6, 96.03) * mm, "end": v(28.03, 91.54) * mm});
            skLineSegment(sketch, "E534.6.3.0", {"start": v(34.84, 93.93) * mm, "end": v(32.7, 88.22) * mm});
            skLineSegment(sketch, "E534.9.3.0", {"start": v(36.92, 88.22) * mm, "end": v(30.34, 81.36) * mm});
            skLineSegment(sketch, "E534.12.3.0", {"start": v(29.8, 89.73) * mm, "end": v(34.84, 93.93) * mm});
            skLineSegment(sketch, "E534.15.3.0", {"start": v(27.3, 90.59) * mm, "end": v(22.33, 85.19) * mm});
            skLineSegment(sketch, "E534.18.3.0", {"start": v(20.1, 92.03) * mm, "end": v(26.62, 98.35) * mm});
            skLineSegment(sketch, "E534.21.3.0", {"start": v(29.71, 85.36) * mm, "end": v(24.03, 83.75) * mm});
            skLineSegment(sketch, "E534.24.3.0", {"start": v(22.33, 85.19) * mm, "end": v(23.96, 91.9) * mm});
            skLineSegment(sketch, "E534.27.3.0", {"start": v(26.62, 94.56) * mm, "end": v(32.6, 96.03) * mm});
            skLineSegment(sketch, "E534.30.3.0", {"start": v(32.7, 88.22) * mm, "end": v(36.92, 88.22) * mm});
            skLineSegment(sketch, "E534.33.3.0", {"start": v(23.96, 91.9) * mm, "end": v(20.1, 92.03) * mm});
            skLineSegment(sketch, "E534.36.3.0", {"start": v(30.34, 81.36) * mm, "end": v(29.71, 85.36) * mm});
            skLineSegment(sketch, "E534.39.3.0", {"start": v(28.03, 91.54) * mm, "end": v(29.8, 89.73) * mm});
            skLineSegment(sketch, "E534.42.3.0", {"start": v(26.62, 98.35) * mm, "end": v(26.62, 94.56) * mm});
            skLineSegment(sketch, "E534.45.3.0", {"start": v(28.94, 89.08) * mm, "end": v(27.3, 90.59) * mm});
            skLineSegment(sketch, "E534.0.3.1", {"start": v(24.03, 64.19) * mm, "end": v(28.94, 69.52) * mm});
            skLineSegment(sketch, "E534.3.3.1", {"start": v(32.6, 76.47) * mm, "end": v(28.03, 71.98) * mm});
            skLineSegment(sketch, "E534.6.3.1", {"start": v(34.84, 74.37) * mm, "end": v(32.7, 68.66) * mm});
            skLineSegment(sketch, "E534.9.3.1", {"start": v(36.92, 68.66) * mm, "end": v(30.34, 61.8) * mm});
            skLineSegment(sketch, "E534.12.3.1", {"start": v(29.8, 70.18) * mm, "end": v(34.84, 74.37) * mm});
            skLineSegment(sketch, "E534.15.3.1", {"start": v(27.3, 71.03) * mm, "end": v(22.33, 65.63) * mm});
            skLineSegment(sketch, "E534.18.3.1", {"start": v(20.1, 72.47) * mm, "end": v(26.62, 78.8) * mm});
            skLineSegment(sketch, "E534.21.3.1", {"start": v(29.71, 65.8) * mm, "end": v(24.03, 64.19) * mm});
            skLineSegment(sketch, "E534.24.3.1", {"start": v(22.33, 65.63) * mm, "end": v(23.96, 72.33) * mm});
            skLineSegment(sketch, "E534.27.3.1", {"start": v(26.62, 75) * mm, "end": v(32.6, 76.47) * mm});
            skLineSegment(sketch, "E534.30.3.1", {"start": v(32.7, 68.66) * mm, "end": v(36.92, 68.66) * mm});
            skLineSegment(sketch, "E534.33.3.1", {"start": v(23.96, 72.33) * mm, "end": v(20.1, 72.47) * mm});
            skLineSegment(sketch, "E534.36.3.1", {"start": v(30.34, 61.8) * mm, "end": v(29.71, 65.8) * mm});
            skLineSegment(sketch, "E534.39.3.1", {"start": v(28.03, 71.98) * mm, "end": v(29.8, 70.18) * mm});
            skLineSegment(sketch, "E534.42.3.1", {"start": v(26.62, 78.8) * mm, "end": v(26.62, 75) * mm});
            skLineSegment(sketch, "E534.45.3.1", {"start": v(28.94, 69.52) * mm, "end": v(27.3, 71.03) * mm});
            skLineSegment(sketch, "E534.0.3.2", {"start": v(24.03, 44.63) * mm, "end": v(28.94, 49.97) * mm});
            skLineSegment(sketch, "E534.3.3.2", {"start": v(32.6, 56.92) * mm, "end": v(28.03, 52.42) * mm});
            skLineSegment(sketch, "E534.6.3.2", {"start": v(34.84, 54.81) * mm, "end": v(32.7, 49.1) * mm});
            skLineSegment(sketch, "E534.9.3.2", {"start": v(36.92, 49.1) * mm, "end": v(30.34, 42.24) * mm});
            skLineSegment(sketch, "E534.12.3.2", {"start": v(29.8, 50.62) * mm, "end": v(34.84, 54.81) * mm});
            skLineSegment(sketch, "E534.15.3.2", {"start": v(27.3, 51.47) * mm, "end": v(22.33, 46.07) * mm});
            skLineSegment(sketch, "E534.18.3.2", {"start": v(20.1, 52.91) * mm, "end": v(26.62, 59.23) * mm});
            skLineSegment(sketch, "E534.21.3.2", {"start": v(29.71, 46.25) * mm, "end": v(24.03, 44.63) * mm});
            skLineSegment(sketch, "E534.24.3.2", {"start": v(22.33, 46.07) * mm, "end": v(23.96, 52.77) * mm});
            skLineSegment(sketch, "E534.27.3.2", {"start": v(26.62, 55.44) * mm, "end": v(32.6, 56.92) * mm});
            skLineSegment(sketch, "E534.30.3.2", {"start": v(32.7, 49.1) * mm, "end": v(36.92, 49.1) * mm});
            skLineSegment(sketch, "E534.33.3.2", {"start": v(23.96, 52.77) * mm, "end": v(20.1, 52.91) * mm});
            skLineSegment(sketch, "E534.36.3.2", {"start": v(30.34, 42.24) * mm, "end": v(29.71, 46.25) * mm});
            skLineSegment(sketch, "E534.39.3.2", {"start": v(28.03, 52.42) * mm, "end": v(29.8, 50.62) * mm});
            skLineSegment(sketch, "E534.42.3.2", {"start": v(26.62, 59.23) * mm, "end": v(26.62, 55.44) * mm});
            skLineSegment(sketch, "E534.45.3.2", {"start": v(28.94, 49.97) * mm, "end": v(27.3, 51.47) * mm});
            skLineSegment(sketch, "E534.0.3.3", {"start": v(24.03, 25.07) * mm, "end": v(28.94, 30.4) * mm});
            skLineSegment(sketch, "E534.3.3.3", {"start": v(32.6, 37.36) * mm, "end": v(28.03, 32.87) * mm});
            skLineSegment(sketch, "E534.6.3.3", {"start": v(34.84, 35.25) * mm, "end": v(32.7, 29.54) * mm});
            skLineSegment(sketch, "E534.9.3.3", {"start": v(36.92, 29.54) * mm, "end": v(30.34, 22.69) * mm});
            skLineSegment(sketch, "E534.12.3.3", {"start": v(29.8, 31.06) * mm, "end": v(34.84, 35.25) * mm});
            skLineSegment(sketch, "E534.15.3.3", {"start": v(27.3, 31.92) * mm, "end": v(22.33, 26.52) * mm});
            skLineSegment(sketch, "E534.18.3.3", {"start": v(20.1, 33.36) * mm, "end": v(26.62, 39.67) * mm});
            skLineSegment(sketch, "E534.21.3.3", {"start": v(29.71, 26.69) * mm, "end": v(24.03, 25.07) * mm});
            skLineSegment(sketch, "E534.24.3.3", {"start": v(22.33, 26.52) * mm, "end": v(23.96, 33.22) * mm});
            skLineSegment(sketch, "E534.27.3.3", {"start": v(26.62, 35.88) * mm, "end": v(32.6, 37.36) * mm});
            skLineSegment(sketch, "E534.30.3.3", {"start": v(32.7, 29.54) * mm, "end": v(36.92, 29.54) * mm});
            skLineSegment(sketch, "E534.33.3.3", {"start": v(23.96, 33.22) * mm, "end": v(20.1, 33.36) * mm});
            skLineSegment(sketch, "E534.36.3.3", {"start": v(30.34, 22.69) * mm, "end": v(29.71, 26.69) * mm});
            skLineSegment(sketch, "E534.39.3.3", {"start": v(28.03, 32.87) * mm, "end": v(29.8, 31.06) * mm});
            skLineSegment(sketch, "E534.42.3.3", {"start": v(26.62, 39.67) * mm, "end": v(26.62, 35.88) * mm});
            skLineSegment(sketch, "E534.45.3.3", {"start": v(28.94, 30.4) * mm, "end": v(27.3, 31.92) * mm});
            skLineSegment(sketch, "E535.0.0.4", {"start": v(-33.12, 5.51) * mm, "end": v(-28.21, 10.85) * mm});
            skLineSegment(sketch, "E535.3.0.4", {"start": v(-24.56, 17.8) * mm, "end": v(-29.12, 13.3) * mm});
            skLineSegment(sketch, "E535.6.0.4", {"start": v(-22.31, 15.7) * mm, "end": v(-24.45, 9.99) * mm});
            skLineSegment(sketch, "E535.9.0.4", {"start": v(-20.23, 9.99) * mm, "end": v(-26.8, 3.13) * mm});
            skLineSegment(sketch, "E535.12.0.4", {"start": v(-27.35, 11.5) * mm, "end": v(-22.31, 15.7) * mm});
            skLineSegment(sketch, "E535.15.0.4", {"start": v(-29.85, 12.36) * mm, "end": v(-34.82, 6.96) * mm});
            skLineSegment(sketch, "E535.18.0.4", {"start": v(-37.06, 13.8) * mm, "end": v(-30.53, 20.12) * mm});
            skLineSegment(sketch, "E535.21.0.4", {"start": v(-27.44, 7.13) * mm, "end": v(-33.12, 5.51) * mm});
            skLineSegment(sketch, "E535.24.0.4", {"start": v(-34.82, 6.96) * mm, "end": v(-33.2, 13.66) * mm});
            skLineSegment(sketch, "E535.27.0.4", {"start": v(-30.53, 16.33) * mm, "end": v(-24.56, 17.8) * mm});
            skLineSegment(sketch, "E535.30.0.4", {"start": v(-24.45, 9.99) * mm, "end": v(-20.23, 9.99) * mm});
            skLineSegment(sketch, "E535.33.0.4", {"start": v(-33.2, 13.66) * mm, "end": v(-37.06, 13.8) * mm});
            skLineSegment(sketch, "E535.36.0.4", {"start": v(-26.8, 3.13) * mm, "end": v(-27.44, 7.13) * mm});
            skLineSegment(sketch, "E535.39.0.4", {"start": v(-29.12, 13.3) * mm, "end": v(-27.35, 11.5) * mm});
            skLineSegment(sketch, "E535.42.0.4", {"start": v(-30.53, 20.12) * mm, "end": v(-30.53, 16.33) * mm});
            skLineSegment(sketch, "E535.45.0.4", {"start": v(-28.21, 10.85) * mm, "end": v(-29.85, 12.36) * mm});
            skLineSegment(sketch, "E535.0.1.4", {"start": v(-14.07, 5.51) * mm, "end": v(-9.16, 10.85) * mm});
            skLineSegment(sketch, "E535.3.1.4", {"start": v(-5.5, 17.8) * mm, "end": v(-10.07, 13.3) * mm});
            skLineSegment(sketch, "E535.6.1.4", {"start": v(-3.26, 15.7) * mm, "end": v(-5.4, 9.99) * mm});
            skLineSegment(sketch, "E535.9.1.4", {"start": v(-1.18, 9.99) * mm, "end": v(-7.76, 3.13) * mm});
            skLineSegment(sketch, "E535.12.1.4", {"start": v(-8.3, 11.5) * mm, "end": v(-3.26, 15.7) * mm});
            skLineSegment(sketch, "E535.15.1.4", {"start": v(-10.8, 12.36) * mm, "end": v(-15.77, 6.96) * mm});
            skLineSegment(sketch, "E535.18.1.4", {"start": v(-18, 13.8) * mm, "end": v(-11.48, 20.12) * mm});
            skLineSegment(sketch, "E535.21.1.4", {"start": v(-8.39, 7.13) * mm, "end": v(-14.07, 5.51) * mm});
            skLineSegment(sketch, "E535.24.1.4", {"start": v(-15.77, 6.96) * mm, "end": v(-14.14, 13.66) * mm});
            skLineSegment(sketch, "E535.27.1.4", {"start": v(-11.48, 16.33) * mm, "end": v(-5.5, 17.8) * mm});
            skLineSegment(sketch, "E535.30.1.4", {"start": v(-5.4, 9.99) * mm, "end": v(-1.18, 9.99) * mm});
            skLineSegment(sketch, "E535.33.1.4", {"start": v(-14.14, 13.66) * mm, "end": v(-18, 13.8) * mm});
            skLineSegment(sketch, "E535.36.1.4", {"start": v(-7.76, 3.13) * mm, "end": v(-8.39, 7.13) * mm});
            skLineSegment(sketch, "E535.39.1.4", {"start": v(-10.07, 13.3) * mm, "end": v(-8.3, 11.5) * mm});
            skLineSegment(sketch, "E535.42.1.4", {"start": v(-11.48, 20.12) * mm, "end": v(-11.48, 16.33) * mm});
            skLineSegment(sketch, "E535.45.1.4", {"start": v(-9.16, 10.85) * mm, "end": v(-10.8, 12.36) * mm});
            skLineSegment(sketch, "E535.0.2.4", {"start": v(4.98, 5.51) * mm, "end": v(9.89, 10.85) * mm});
            skLineSegment(sketch, "E535.3.2.4", {"start": v(13.54, 17.8) * mm, "end": v(8.98, 13.3) * mm});
            skLineSegment(sketch, "E535.6.2.4", {"start": v(15.79, 15.7) * mm, "end": v(13.65, 9.99) * mm});
            skLineSegment(sketch, "E535.9.2.4", {"start": v(17.87, 9.99) * mm, "end": v(11.3, 3.13) * mm});
            skLineSegment(sketch, "E535.12.2.4", {"start": v(10.75, 11.5) * mm, "end": v(15.79, 15.7) * mm});
            skLineSegment(sketch, "E535.15.2.4", {"start": v(8.25, 12.36) * mm, "end": v(3.28, 6.96) * mm});
            skLineSegment(sketch, "E535.18.2.4", {"start": v(1.04, 13.8) * mm, "end": v(7.57, 20.12) * mm});
            skLineSegment(sketch, "E535.21.2.4", {"start": v(10.66, 7.13) * mm, "end": v(4.98, 5.51) * mm});
            skLineSegment(sketch, "E535.24.2.4", {"start": v(3.28, 6.96) * mm, "end": v(4.9, 13.66) * mm});
            skLineSegment(sketch, "E535.27.2.4", {"start": v(7.57, 16.33) * mm, "end": v(13.54, 17.8) * mm});
            skLineSegment(sketch, "E535.30.2.4", {"start": v(13.65, 9.99) * mm, "end": v(17.87, 9.99) * mm});
            skLineSegment(sketch, "E535.33.2.4", {"start": v(4.9, 13.66) * mm, "end": v(1.04, 13.8) * mm});
            skLineSegment(sketch, "E535.36.2.4", {"start": v(11.3, 3.13) * mm, "end": v(10.66, 7.13) * mm});
            skLineSegment(sketch, "E535.39.2.4", {"start": v(8.98, 13.3) * mm, "end": v(10.75, 11.5) * mm});
            skLineSegment(sketch, "E535.42.2.4", {"start": v(7.57, 20.12) * mm, "end": v(7.57, 16.33) * mm});
            skLineSegment(sketch, "E535.45.2.4", {"start": v(9.89, 10.85) * mm, "end": v(8.25, 12.36) * mm});
            skLineSegment(sketch, "E535.0.3.4", {"start": v(24.03, 5.51) * mm, "end": v(28.94, 10.85) * mm});
            skLineSegment(sketch, "E535.3.3.4", {"start": v(32.6, 17.8) * mm, "end": v(28.03, 13.3) * mm});
            skLineSegment(sketch, "E535.6.3.4", {"start": v(34.84, 15.7) * mm, "end": v(32.7, 9.99) * mm});
            skLineSegment(sketch, "E535.9.3.4", {"start": v(36.92, 9.99) * mm, "end": v(30.34, 3.13) * mm});
            skLineSegment(sketch, "E535.12.3.4", {"start": v(29.8, 11.5) * mm, "end": v(34.84, 15.7) * mm});
            skLineSegment(sketch, "E535.15.3.4", {"start": v(27.3, 12.36) * mm, "end": v(22.33, 6.96) * mm});
            skLineSegment(sketch, "E535.18.3.4", {"start": v(20.1, 13.8) * mm, "end": v(26.62, 20.12) * mm});
            skLineSegment(sketch, "E535.21.3.4", {"start": v(29.71, 7.13) * mm, "end": v(24.03, 5.51) * mm});
            skLineSegment(sketch, "E535.24.3.4", {"start": v(22.33, 6.96) * mm, "end": v(23.96, 13.66) * mm});
            skLineSegment(sketch, "E535.27.3.4", {"start": v(26.62, 16.33) * mm, "end": v(32.6, 17.8) * mm});
            skLineSegment(sketch, "E535.30.3.4", {"start": v(32.7, 9.99) * mm, "end": v(36.92, 9.99) * mm});
            skLineSegment(sketch, "E535.33.3.4", {"start": v(23.96, 13.66) * mm, "end": v(20.1, 13.8) * mm});
            skLineSegment(sketch, "E535.36.3.4", {"start": v(30.34, 3.13) * mm, "end": v(29.71, 7.13) * mm});
            skLineSegment(sketch, "E535.39.3.4", {"start": v(28.03, 13.3) * mm, "end": v(29.8, 11.5) * mm});
            skLineSegment(sketch, "E535.42.3.4", {"start": v(26.62, 20.12) * mm, "end": v(26.62, 16.33) * mm});
            skLineSegment(sketch, "E535.45.3.4", {"start": v(28.94, 10.85) * mm, "end": v(27.3, 12.36) * mm});
            skSolve(sketch);
        }
        {
            var Q0;
            Q0 = qSketchRegion(id + "F12", true);
            extrude(context, id + "F13", {"entities" : qUnion([Q0]), "operationType" : NewBodyOperationType.REMOVE, "oppositeDirection" : true, "depth" : 228.6 * mm, "offsetDistance" : 25.4 * mm});
        }
        {
            var Q0;
            Q0=makeQuery(id+"F4.opExtrude","SWEPT_FACE",FACE,{"disambiguationData":[OSD([sQuery(id+"F3.wireOp",EDGE,"E5.left")])]});
            var sketch = newSketch(context, id + "F14", { "sketchPlane" : qUnion([Q0])});
            skLineSegment(sketch, "E536", {"start": v(0, 111.13) * mm, "end": v(0, 101.6) * mm, "construction": true});
            skLineSegment(sketch, "E537", {"start": v(-38.1, 106.36) * mm, "end": v(38.1, 106.36) * mm, "construction": true});
            skCircle(sketch, "E538", {"center": v(0, 106.36) * mm, "radius": 1.59 * mm});
            skCircle(sketch, "E539", {"center": v(-16.51, 106.36) * mm, "radius": 1.59 * mm});
            skCircle(sketch, "E540", {"center": v(16.5, 106.36) * mm, "radius": 1.59 * mm});
            skCircle(sketch, "E541", {"center": v(-33.02, 106.36) * mm, "radius": 1.59 * mm});
            skCircle(sketch, "E542", {"center": v(33.02, 106.36) * mm, "radius": 1.59 * mm});
            skLineSegment(sketch, "E543", {"start": v(-38.1, 0) * mm, "end": v(-38.1, 101.6) * mm, "construction": true});
            skLineSegment(sketch, "E544", {"start": v(-38.1, 101.6) * mm, "end": v(-38.1, 0) * mm, "construction": true});
            skLineSegment(sketch, "E545", {"start": v(38.1, 101.6) * mm, "end": v(38.1, 0) * mm, "construction": true});
            skLineSegment(sketch, "E546", {"start": v(38.1, 0) * mm, "end": v(38.1, 101.6) * mm, "construction": true});
            skLineSegment(sketch, "E547", {"start": v(-38.1, 50.8) * mm, "end": v(38.1, 50.8) * mm, "construction": true});
            skCircle(sketch, "E548.MirrorC", {"center": v(33.02, -4.76) * mm, "radius": 1.59 * mm});
            skCircle(sketch, "E549.MirrorC", {"center": v(16.5, -4.76) * mm, "radius": 1.59 * mm});
            skCircle(sketch, "E550.MirrorC", {"center": v(0, -4.76) * mm, "radius": 1.59 * mm});
            skCircle(sketch, "E551.MirrorC", {"center": v(-16.51, -4.76) * mm, "radius": 1.59 * mm});
            skCircle(sketch, "E552.MirrorC", {"center": v(-33.02, -4.76) * mm, "radius": 1.59 * mm});
            skSolve(sketch);
        }
        {
            var Q0;
            Q0 = qSketchRegion(id + "F14", true);
            extrude(context, id + "F15", {"entities" : qUnion([Q0]), "operationType" : NewBodyOperationType.REMOVE, "oppositeDirection" : true, "depth" : 228.6 * mm, "offsetDistance" : 25.4 * mm});
        }
        {
            var Q0;
            Q0=makeQuery(id+"F1.opExtrude","SWEPT_FACE",FACE,{"disambiguationData":[OSD([sQuery(id+"F0.wireOp",EDGE,"E2.filletArc")])]});
            cPlane(context, id + "F16", {"entities" : qUnion([Q0]), "cplaneType" : CPlaneType.LINE_ANGLE, "offset" : 25.4 * mm, "angle" : 45 * degree, "width" : 152.4 * mm, "height" : 152.4 * mm});
        }
        {
            var Q0;
            Q0=qCreatedBy(id+"F16.planeOp",FACE);
            var sketch = newSketch(context, id + "F17", { "sketchPlane" : qUnion([Q0])});
            skLineSegment(sketch, "E553", {"start": v(-44.94, 0) * mm, "end": v(-26.56, 0) * mm});
            skPoint(sketch, "E554", {"position": v(-35.75, 0) * mm});
            skLineSegment(sketch, "E555", {"start": v(-35.75, 0) * mm, "end": v(-35.75, -9.46) * mm, "construction": true});
            skCircle(sketch, "E556", {"center": v(-35.75, -4.73) * mm, "radius": 1.59 * mm});
            skPoint(sketch, "E557", {"position": v(-35.92, 101.7) * mm});
            skLineSegment(sketch, "E558", {"start": v(-35.92, 101.7) * mm, "end": v(-35.92, 111.13) * mm, "construction": true});
            skCircle(sketch, "E559", {"center": v(-35.92, 106.4) * mm, "radius": 1.59 * mm});
            skSolve(sketch);
        }
        {
            var Q0;
            Q0 = qSketchRegion(id + "F17", true);
            extrude(context, id + "F18", {"entities" : qUnion([Q0]), "operationType" : NewBodyOperationType.REMOVE, "oppositeDirection" : true, "depth" : 50.8 * mm, "offsetDistance" : 25.4 * mm});
        }
        {
            var Q0;
            Q0=makeQuery(id+"F1.opExtrude","CAP_EDGE",EDGE,{"disambiguationData":[OSD([sQuery(id+"F0.wireOp",EDGE,"E1.filletArc")])],"isStart":false});
            cPoint(context, id + "F19", {"entities" : qUnion([Q0]), "parameter" : 0.5});
        }
        {
            var Q0;
            Q0=makeQuery(id+"F1.opExtrude","SWEPT_FACE",FACE,{"disambiguationData":[OSD([sQuery(id+"F0.wireOp",EDGE,"E1.filletArc")])]});
            var Q1;
            Q1 = qCreatedBy(id + "F19" ,VERTEX);
            cPlane(context, id + "F20", {"entities" : qUnion([Q0, Q1]), "cplaneType" : CPlaneType.LINE_ANGLE, "offset" : 25.4 * mm, "angle" : 90 * degree, "oppositeDirection" : true, "width" : 152.4 * mm, "height" : 152.4 * mm});
        }
        {
            var Q0;
            Q0=qCreatedBy(id+"F20.planeOp",FACE);
            var sketch = newSketch(context, id + "F21", { "sketchPlane" : qUnion([Q0])});
            skLineSegment(sketch, "E560", {"start": v(-44.95, 0) * mm, "end": v(-26.97, 0) * mm, "construction": true});
            skLineSegment(sketch, "E561", {"start": v(-35.96, 0) * mm, "end": v(-35.96, -9.52) * mm, "construction": true});
            skCircle(sketch, "E562", {"center": v(-35.96, -4.76) * mm, "radius": 1.59 * mm});
            skLineSegment(sketch, "E563", {"start": v(-35.96, 111.2) * mm, "end": v(-35.96, 101.65) * mm, "construction": true});
            skCircle(sketch, "E564", {"center": v(-35.96, 106.42) * mm, "radius": 1.59 * mm});
            skSolve(sketch);
        }
        {
            var Q0;
            Q0 = qSketchRegion(id + "F21", true);
            extrude(context, id + "F22", {"entities" : qUnion([Q0]), "operationType" : NewBodyOperationType.REMOVE, "depth" : 50.8 * mm, "offsetDistance" : 25.4 * mm});
        }
        {
            var Q0;
            Q0=qCreatedBy(id+"F16.planeOp",FACE);
            cPlane(context, id + "F23", {"entities" : qUnion([Q0]), "cplaneType" : CPlaneType.OFFSET, "offset" : 177.8 * mm, "width" : 152.4 * mm, "height" : 152.4 * mm});
        }
        {
            var Q0;
            Q0=qCreatedBy(id+"F23.planeOp",FACE);
            var sketch = newSketch(context, id + "F24", { "sketchPlane" : qUnion([Q0])});
            skLineSegment(sketch, "E565", {"start": v(26.95, 0) * mm, "end": v(44.9, 0) * mm, "construction": true});
            skLineSegment(sketch, "E566", {"start": v(35.93, 0) * mm, "end": v(35.93, -9.44) * mm, "construction": true});
            skCircle(sketch, "E567", {"center": v(35.93, -4.72) * mm, "radius": 1.59 * mm});
            skLineSegment(sketch, "E568", {"start": v(35.93, 111.22) * mm, "end": v(35.93, 101.61) * mm, "construction": true});
            skCircle(sketch, "E569", {"center": v(35.93, 106.42) * mm, "radius": 1.59 * mm});
            skSolve(sketch);
        }
        {
            var Q0;
            Q0 = qSketchRegion(id + "F24", true);
            extrude(context, id + "F25", {"entities" : qUnion([Q0]), "operationType" : NewBodyOperationType.REMOVE, "depth" : 76.2 * mm, "offsetDistance" : 25.4 * mm});
        }
        {
            var Q0;
            Q0=qCreatedBy(id+"F20.planeOp",FACE);
            cPlane(context, id + "F26", {"entities" : qUnion([Q0]), "cplaneType" : CPlaneType.OFFSET, "offset" : 177.8 * mm, "oppositeDirection" : true, "width" : 152.4 * mm, "height" : 152.4 * mm});
        }
        {
            var Q0;
            Q0=qCreatedBy(id+"F26.planeOp",FACE);
            var sketch = newSketch(context, id + "F27", { "sketchPlane" : qUnion([Q0])});
            skLineSegment(sketch, "E570", {"start": v(26.9, 101.67) * mm, "end": v(44.94, 101.67) * mm, "construction": true});
            skLineSegment(sketch, "E571", {"start": v(35.92, 101.67) * mm, "end": v(35.92, 111.22) * mm, "construction": true});
            skCircle(sketch, "E572", {"center": v(35.92, 106.44) * mm, "radius": 1.59 * mm});
            skLineSegment(sketch, "E573", {"start": v(35.92, 0) * mm, "end": v(35.92, -9.55) * mm, "construction": true});
            skCircle(sketch, "E574", {"center": v(35.92, -4.77) * mm, "radius": 1.59 * mm});
            skSolve(sketch);
        }
        {
            var Q0;
            Q0 = qSketchRegion(id + "F27", true);
            extrude(context, id + "F28", {"entities" : qUnion([Q0]), "operationType" : NewBodyOperationType.REMOVE, "oppositeDirection" : true, "depth" : 76.2 * mm, "offsetDistance" : 25.4 * mm});
        }
    });
